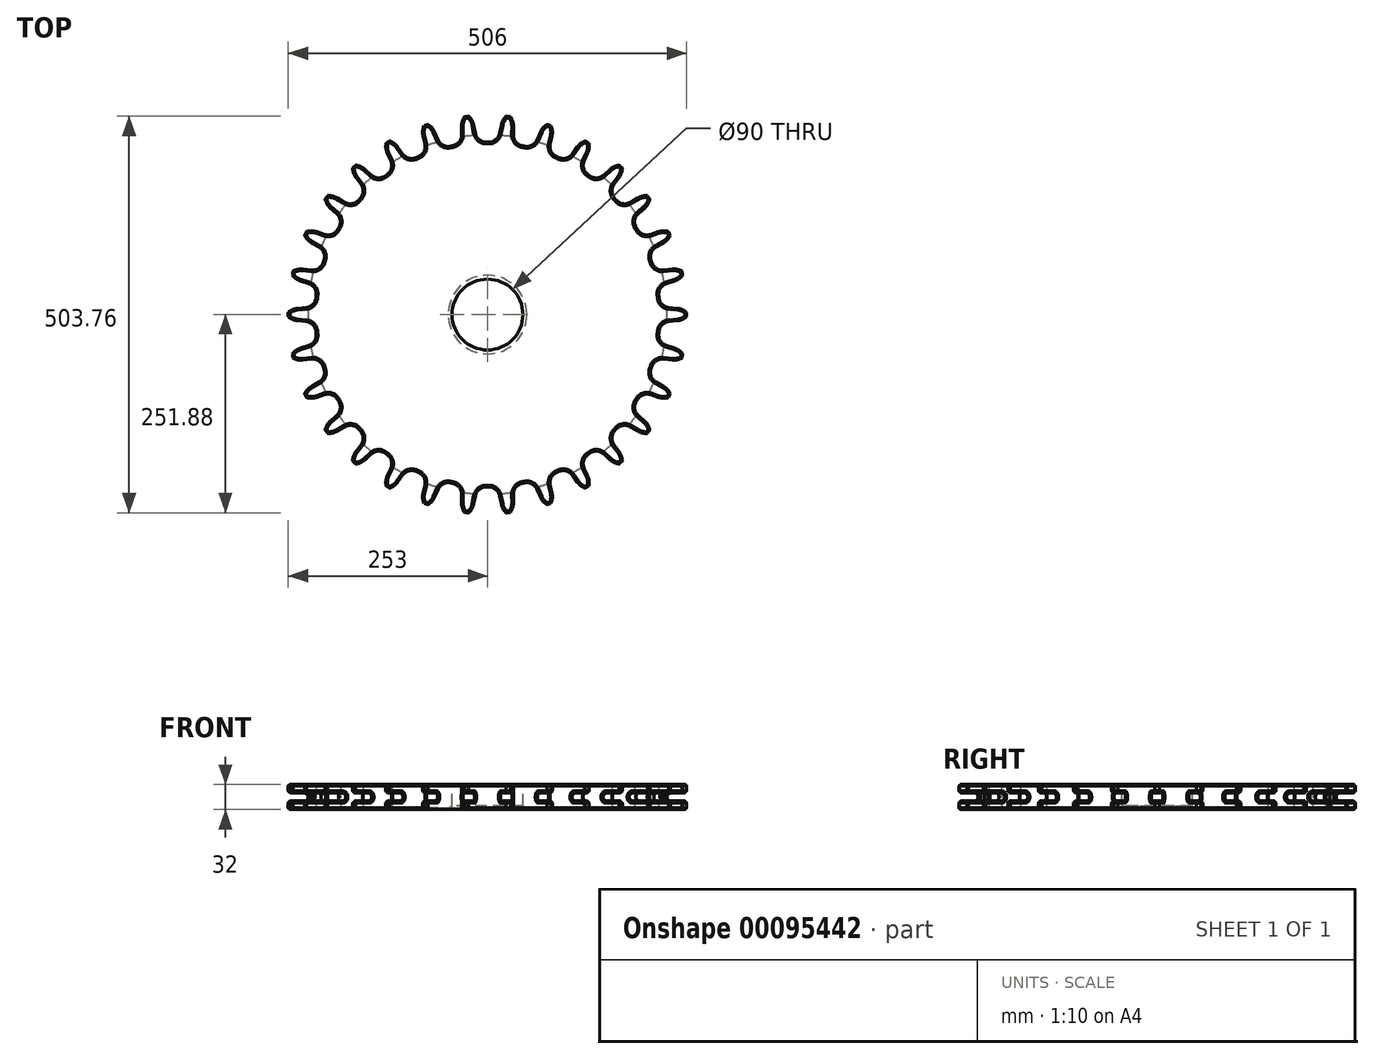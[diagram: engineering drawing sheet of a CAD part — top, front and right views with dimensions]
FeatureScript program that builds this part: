
annotation { "Feature Type Name" : "Feature", "Feature Type Description" : "" }
export const myFeature = defineFeature(function(context is Context, id is Id, definition is map)
    precondition{}
    {
        {
            var Q0;
            Q0=qCreatedBy(makeId("Top.planeOp"),FACE);
            var sketch = newSketch(context, id + "F0", { "sketchPlane" : qUnion([Q0])});
            skCircle(sketch, "E0", {"center": v(0, 0) * mm, "radius": 253 * mm});
            skCircle(sketch, "E1", {"center": v(0, 0) * mm, "radius": 216.9 * mm, "construction": true});
            skLineSegment(sketch, "E2", {"start": v(0, 0) * mm, "end": v(253, 0) * mm, "construction": true});
            skLineSegment(sketch, "E3", {"start": v(0, 0) * mm, "end": v(252.65, -13.34) * mm, "construction": true});
            skCircle(sketch, "E4", {"center": v(0, 0) * mm, "radius": 239.77 * mm, "construction": true});
            skCircle(sketch, "E5", {"center": v(239.43, -12.64) * mm, "radius": 20.44 * mm});
            skLineSegment(sketch, "E6", {"start": v(0, 0) * mm, "end": v(251.8, 24.61) * mm, "construction": true});
            skCircle(sketch, "E7", {"center": v(0, 0) * mm, "radius": 232.9 * mm, "construction": true});
            skCircle(sketch, "E8", {"center": v(231.8, 22.66) * mm, "radius": 14 * mm});
            skLineSegment(sketch, "E9", {"start": v(230.5, 8.72) * mm, "end": v(241.32, 7.72) * mm});
            skCircle(sketch, "E10", {"center": v(0, 0) * mm, "radius": 218.9 * mm});
            skSolve(sketch);
        }
        {
            var Q0;
            Q0=qCreatedBy(makeId("Top.planeOp"),FACE);
            var sketch = newSketch(context, id + "F1", { "sketchPlane" : qUnion([Q0])});
            skArc(sketch, "E11.0", {"start": v(217.86, 21.3) * mm, "mid": v(221.92, 12.73) * mm, "end": v(230.5, 8.72) * mm});
            skArc(sketch, "E12.0", {"start": v(252.99, 2.67) * mm, "mid": v(247.56, 6.12) * mm, "end": v(241.32, 7.72) * mm});
            skArc(sketch, "E13.0", {"start": v(253, 0) * mm, "mid": v(253, 1.33) * mm, "end": v(252.99, 2.67) * mm});
            skLineSegment(sketch, "E14.0", {"start": v(0, 0) * mm, "end": v(253, 0) * mm, "construction": true});
            skLineSegment(sketch, "E15.0", {"start": v(230.5, 8.72) * mm, "end": v(241.32, 7.72) * mm});
            skArc(sketch, "E16.MirrorCS", {"start": v(253, 0) * mm, "mid": v(253, -1.33) * mm, "end": v(252.99, -2.67) * mm});
            skArc(sketch, "E17.MirrorCS", {"start": v(252.99, -2.67) * mm, "mid": v(247.56, -6.12) * mm, "end": v(241.32, -7.72) * mm});
            skLineSegment(sketch, "E18.MirrorCS", {"start": v(230.5, -8.72) * mm, "end": v(241.32, -7.72) * mm});
            skArc(sketch, "E19.MirrorCS", {"start": v(217.86, -21.3) * mm, "mid": v(221.92, -12.73) * mm, "end": v(230.5, -8.72) * mm});
            skLineSegment(sketch, "E20.1.0", {"start": v(0, 0) * mm, "end": v(247.47, 52.6) * mm, "construction": true});
            skArc(sketch, "E20.1.1", {"start": v(208.68, 66.13) * mm, "mid": v(214.43, 58.6) * mm, "end": v(223.66, 56.45) * mm});
            skLineSegment(sketch, "E20.1.2", {"start": v(223.66, 56.45) * mm, "end": v(234.44, 57.72) * mm});
            skArc(sketch, "E20.1.3", {"start": v(246.9, 55.2) * mm, "mid": v(240.87, 57.46) * mm, "end": v(234.44, 57.72) * mm});
            skArc(sketch, "E20.1.4", {"start": v(247.47, 52.6) * mm, "mid": v(247.2, 53.9) * mm, "end": v(246.9, 55.2) * mm});
            skArc(sketch, "E20.1.5", {"start": v(247.47, 52.6) * mm, "mid": v(247.75, 51.3) * mm, "end": v(248.01, 50) * mm});
            skArc(sketch, "E20.1.6", {"start": v(248.01, 50) * mm, "mid": v(243.42, 45.48) * mm, "end": v(237.65, 42.63) * mm});
            skLineSegment(sketch, "E20.1.7", {"start": v(227.28, 39.4) * mm, "end": v(237.65, 42.63) * mm});
            skArc(sketch, "E20.1.8", {"start": v(217.53, 24.47) * mm, "mid": v(219.72, 33.68) * mm, "end": v(227.28, 39.4) * mm});
            skLineSegment(sketch, "E20.2.0", {"start": v(0, 0) * mm, "end": v(231.13, 102.9) * mm, "construction": true});
            skArc(sketch, "E20.2.1", {"start": v(190.37, 108.07) * mm, "mid": v(197.56, 101.9) * mm, "end": v(207.03, 101.72) * mm});
            skLineSegment(sketch, "E20.2.2", {"start": v(207.03, 101.72) * mm, "end": v(217.32, 105.2) * mm});
            skArc(sketch, "E20.2.3", {"start": v(230.03, 105.33) * mm, "mid": v(223.66, 106.28) * mm, "end": v(217.32, 105.2) * mm});
            skArc(sketch, "E20.2.4", {"start": v(231.13, 102.9) * mm, "mid": v(230.58, 104.12) * mm, "end": v(230.03, 105.33) * mm});
            skArc(sketch, "E20.2.5", {"start": v(231.13, 102.9) * mm, "mid": v(231.67, 101.69) * mm, "end": v(232.2, 100.46) * mm});
            skArc(sketch, "E20.2.6", {"start": v(232.2, 100.46) * mm, "mid": v(228.64, 95.1) * mm, "end": v(223.6, 91.1) * mm});
            skLineSegment(sketch, "E20.2.7", {"start": v(214.12, 85.8) * mm, "end": v(223.6, 91.1) * mm});
            skArc(sketch, "E20.2.8", {"start": v(207.7, 69.16) * mm, "mid": v(207.92, 78.63) * mm, "end": v(214.12, 85.8) * mm});
            skLineSegment(sketch, "E21.1.3.0", {"start": v(0, 0) * mm, "end": v(204.68, 148.7) * mm, "construction": true});
            skArc(sketch, "E21.3.3.0", {"start": v(163.74, 145.29) * mm, "mid": v(172.06, 140.75) * mm, "end": v(181.36, 142.54) * mm});
            skLineSegment(sketch, "E21.7.3.0", {"start": v(181.36, 142.54) * mm, "end": v(190.7, 148.09) * mm});
            skArc(sketch, "E21.10.3.0", {"start": v(203.1, 150.86) * mm, "mid": v(196.68, 150.46) * mm, "end": v(190.7, 148.09) * mm});
            skArc(sketch, "E21.14.3.0", {"start": v(204.68, 148.7) * mm, "mid": v(203.9, 149.79) * mm, "end": v(203.1, 150.86) * mm});
            skArc(sketch, "E21.18.3.0", {"start": v(204.68, 148.7) * mm, "mid": v(205.46, 147.63) * mm, "end": v(206.24, 146.54) * mm});
            skArc(sketch, "E21.22.3.0", {"start": v(206.24, 146.54) * mm, "mid": v(203.87, 140.56) * mm, "end": v(199.77, 135.6) * mm});
            skLineSegment(sketch, "E21.26.3.0", {"start": v(191.6, 128.44) * mm, "end": v(199.77, 135.6) * mm});
            skArc(sketch, "E21.29.3.0", {"start": v(188.77, 110.83) * mm, "mid": v(187.02, 120.14) * mm, "end": v(191.6, 128.44) * mm});
            skLineSegment(sketch, "E21.1.4.0", {"start": v(0, 0) * mm, "end": v(169.3, 188.02) * mm, "construction": true});
            skArc(sketch, "E21.3.4.0", {"start": v(129.95, 176.16) * mm, "mid": v(139.03, 173.44) * mm, "end": v(147.76, 177.13) * mm});
            skLineSegment(sketch, "E21.7.4.0", {"start": v(147.76, 177.13) * mm, "end": v(155.74, 184.5) * mm});
            skArc(sketch, "E21.10.4.0", {"start": v(167.3, 189.79) * mm, "mid": v(161.1, 188.07) * mm, "end": v(155.74, 184.5) * mm});
            skArc(sketch, "E21.14.4.0", {"start": v(169.3, 188.02) * mm, "mid": v(168.3, 188.9) * mm, "end": v(167.3, 189.79) * mm});
            skArc(sketch, "E21.18.4.0", {"start": v(169.3, 188.02) * mm, "mid": v(170.28, 187.12) * mm, "end": v(171.26, 186.22) * mm});
            skArc(sketch, "E21.22.4.0", {"start": v(171.26, 186.22) * mm, "mid": v(170.2, 179.87) * mm, "end": v(167.2, 174.17) * mm});
            skLineSegment(sketch, "E21.26.4.0", {"start": v(160.72, 165.47) * mm, "end": v(167.2, 174.17) * mm});
            skArc(sketch, "E21.29.4.0", {"start": v(161.6, 147.65) * mm, "mid": v(157.96, 156.4) * mm, "end": v(160.72, 165.47) * mm});
            skLineSegment(sketch, "E21.1.5.0", {"start": v(0, 0) * mm, "end": v(126.5, 219.1) * mm, "construction": true});
            skArc(sketch, "E21.3.5.0", {"start": v(90.49, 199.32) * mm, "mid": v(99.93, 198.56) * mm, "end": v(107.7, 203.98) * mm});
            skLineSegment(sketch, "E21.7.5.0", {"start": v(107.7, 203.98) * mm, "end": v(113.98, 212.85) * mm});
            skArc(sketch, "E21.10.5.0", {"start": v(124.18, 220.43) * mm, "mid": v(118.48, 217.45) * mm, "end": v(113.98, 212.85) * mm});
            skArc(sketch, "E21.14.5.0", {"start": v(126.5, 219.1) * mm, "mid": v(125.34, 219.77) * mm, "end": v(124.18, 220.43) * mm});
            skArc(sketch, "E21.18.5.0", {"start": v(126.5, 219.1) * mm, "mid": v(127.65, 218.43) * mm, "end": v(128.8, 217.76) * mm});
            skArc(sketch, "E21.22.5.0", {"start": v(128.8, 217.76) * mm, "mid": v(129.08, 211.33) * mm, "end": v(127.34, 205.13) * mm});
            skLineSegment(sketch, "E21.26.5.0", {"start": v(122.8, 195.27) * mm, "end": v(127.34, 205.13) * mm});
            skArc(sketch, "E21.29.5.0", {"start": v(127.38, 178.03) * mm, "mid": v(121.99, 185.82) * mm, "end": v(122.8, 195.27) * mm});
            skLineSegment(sketch, "E22.1.6.0", {"start": v(0, 0) * mm, "end": v(78.18, 240.62) * mm, "construction": true});
            skArc(sketch, "E22.3.6.0", {"start": v(47.07, 213.78) * mm, "mid": v(56.47, 215) * mm, "end": v(62.94, 221.92) * mm});
            skLineSegment(sketch, "E22.7.6.0", {"start": v(62.94, 221.92) * mm, "end": v(67.23, 231.9) * mm});
            skArc(sketch, "E22.10.6.0", {"start": v(75.64, 241.43) * mm, "mid": v(70.68, 237.33) * mm, "end": v(67.23, 231.9) * mm});
            skArc(sketch, "E22.14.6.0", {"start": v(78.18, 240.62) * mm, "mid": v(76.91, 241.03) * mm, "end": v(75.64, 241.43) * mm});
            skArc(sketch, "E22.18.6.0", {"start": v(78.18, 240.62) * mm, "mid": v(79.45, 240.2) * mm, "end": v(80.71, 239.78) * mm});
            skArc(sketch, "E22.22.6.0", {"start": v(80.71, 239.78) * mm, "mid": v(82.32, 233.55) * mm, "end": v(81.91, 227.12) * mm});
            skLineSegment(sketch, "E22.26.6.0", {"start": v(79.52, 216.53) * mm, "end": v(81.91, 227.12) * mm});
            skArc(sketch, "E22.29.6.0", {"start": v(87.58, 200.62) * mm, "mid": v(80.69, 207.13) * mm, "end": v(79.52, 216.53) * mm});
            skLineSegment(sketch, "E22.1.7.0", {"start": v(0, 0) * mm, "end": v(26.45, 251.61) * mm, "construction": true});
            skArc(sketch, "E22.3.7.0", {"start": v(1.6, 218.9) * mm, "mid": v(10.53, 222.04) * mm, "end": v(15.42, 230.16) * mm});
            skLineSegment(sketch, "E22.7.7.0", {"start": v(15.42, 230.16) * mm, "end": v(17.55, 240.8) * mm});
            skArc(sketch, "E22.10.7.0", {"start": v(23.8, 251.88) * mm, "mid": v(19.79, 246.84) * mm, "end": v(17.55, 240.8) * mm});
            skArc(sketch, "E22.14.7.0", {"start": v(26.45, 251.61) * mm, "mid": v(25.12, 251.75) * mm, "end": v(23.8, 251.88) * mm});
            skArc(sketch, "E22.18.7.0", {"start": v(26.45, 251.61) * mm, "mid": v(27.77, 251.47) * mm, "end": v(29.1, 251.32) * mm});
            skArc(sketch, "E22.22.7.0", {"start": v(29.1, 251.32) * mm, "mid": v(31.96, 245.56) * mm, "end": v(32.9, 239.2) * mm});
            skLineSegment(sketch, "E22.26.7.0", {"start": v(32.77, 228.33) * mm, "end": v(32.9, 239.2) * mm});
            skArc(sketch, "E22.29.7.0", {"start": v(43.95, 214.45) * mm, "mid": v(35.86, 219.38) * mm, "end": v(32.77, 228.33) * mm});
            skLineSegment(sketch, "E22.1.8.0", {"start": v(0, 0) * mm, "end": v(-26.45, 251.61) * mm, "construction": true});
            skArc(sketch, "E22.3.8.0", {"start": v(-43.95, 214.45) * mm, "mid": v(-35.86, 219.38) * mm, "end": v(-32.77, 228.33) * mm});
            skLineSegment(sketch, "E22.7.8.0", {"start": v(-32.77, 228.33) * mm, "end": v(-32.9, 239.2) * mm});
            skArc(sketch, "E22.10.8.0", {"start": v(-29.1, 251.32) * mm, "mid": v(-31.96, 245.56) * mm, "end": v(-32.9, 239.2) * mm});
            skArc(sketch, "E22.14.8.0", {"start": v(-26.45, 251.61) * mm, "mid": v(-27.77, 251.47) * mm, "end": v(-29.1, 251.32) * mm});
            skArc(sketch, "E22.18.8.0", {"start": v(-26.45, 251.61) * mm, "mid": v(-25.12, 251.75) * mm, "end": v(-23.8, 251.88) * mm});
            skArc(sketch, "E22.22.8.0", {"start": v(-23.8, 251.88) * mm, "mid": v(-19.79, 246.84) * mm, "end": v(-17.55, 240.8) * mm});
            skLineSegment(sketch, "E22.26.8.0", {"start": v(-15.42, 230.16) * mm, "end": v(-17.55, 240.8) * mm});
            skArc(sketch, "E22.29.8.0", {"start": v(-1.6, 218.9) * mm, "mid": v(-10.53, 222.04) * mm, "end": v(-15.42, 230.16) * mm});
            skLineSegment(sketch, "E22.1.9.0", {"start": v(0, 0) * mm, "end": v(-78.18, 240.62) * mm, "construction": true});
            skArc(sketch, "E22.3.9.0", {"start": v(-87.58, 200.62) * mm, "mid": v(-80.69, 207.13) * mm, "end": v(-79.52, 216.53) * mm});
            skLineSegment(sketch, "E22.7.9.0", {"start": v(-79.52, 216.53) * mm, "end": v(-81.91, 227.12) * mm});
            skArc(sketch, "E22.10.9.0", {"start": v(-80.71, 239.78) * mm, "mid": v(-82.32, 233.55) * mm, "end": v(-81.91, 227.12) * mm});
            skArc(sketch, "E22.14.9.0", {"start": v(-78.18, 240.62) * mm, "mid": v(-79.45, 240.2) * mm, "end": v(-80.71, 239.78) * mm});
            skArc(sketch, "E22.18.9.0", {"start": v(-78.18, 240.62) * mm, "mid": v(-76.91, 241.03) * mm, "end": v(-75.64, 241.43) * mm});
            skArc(sketch, "E22.22.9.0", {"start": v(-75.64, 241.43) * mm, "mid": v(-70.68, 237.33) * mm, "end": v(-67.23, 231.9) * mm});
            skLineSegment(sketch, "E22.26.9.0", {"start": v(-62.94, 221.92) * mm, "end": v(-67.23, 231.9) * mm});
            skArc(sketch, "E22.29.9.0", {"start": v(-47.07, 213.78) * mm, "mid": v(-56.47, 215) * mm, "end": v(-62.94, 221.92) * mm});
            skLineSegment(sketch, "E22.1.10.0", {"start": v(0, 0) * mm, "end": v(-126.5, 219.1) * mm, "construction": true});
            skArc(sketch, "E22.3.10.0", {"start": v(-127.38, 178.03) * mm, "mid": v(-121.99, 185.82) * mm, "end": v(-122.8, 195.27) * mm});
            skLineSegment(sketch, "E22.7.10.0", {"start": v(-122.8, 195.27) * mm, "end": v(-127.34, 205.13) * mm});
            skArc(sketch, "E22.10.10.0", {"start": v(-128.8, 217.76) * mm, "mid": v(-129.08, 211.33) * mm, "end": v(-127.34, 205.13) * mm});
            skArc(sketch, "E22.14.10.0", {"start": v(-126.5, 219.1) * mm, "mid": v(-127.65, 218.43) * mm, "end": v(-128.8, 217.76) * mm});
            skArc(sketch, "E22.18.10.0", {"start": v(-126.5, 219.1) * mm, "mid": v(-125.34, 219.77) * mm, "end": v(-124.18, 220.43) * mm});
            skArc(sketch, "E22.22.10.0", {"start": v(-124.18, 220.43) * mm, "mid": v(-118.48, 217.45) * mm, "end": v(-113.98, 212.85) * mm});
            skLineSegment(sketch, "E22.26.10.0", {"start": v(-107.7, 203.98) * mm, "end": v(-113.98, 212.85) * mm});
            skArc(sketch, "E22.29.10.0", {"start": v(-90.49, 199.32) * mm, "mid": v(-99.93, 198.56) * mm, "end": v(-107.7, 203.98) * mm});
            skLineSegment(sketch, "E22.1.11.0", {"start": v(0, 0) * mm, "end": v(-169.3, 188.02) * mm, "construction": true});
            skArc(sketch, "E22.3.11.0", {"start": v(-161.6, 147.65) * mm, "mid": v(-157.96, 156.4) * mm, "end": v(-160.72, 165.47) * mm});
            skLineSegment(sketch, "E22.7.11.0", {"start": v(-160.72, 165.47) * mm, "end": v(-167.2, 174.17) * mm});
            skArc(sketch, "E22.10.11.0", {"start": v(-171.26, 186.22) * mm, "mid": v(-170.2, 179.87) * mm, "end": v(-167.2, 174.17) * mm});
            skArc(sketch, "E22.14.11.0", {"start": v(-169.3, 188.02) * mm, "mid": v(-170.28, 187.12) * mm, "end": v(-171.26, 186.22) * mm});
            skArc(sketch, "E22.18.11.0", {"start": v(-169.3, 188.02) * mm, "mid": v(-168.3, 188.9) * mm, "end": v(-167.3, 189.79) * mm});
            skArc(sketch, "E22.22.11.0", {"start": v(-167.3, 189.79) * mm, "mid": v(-161.1, 188.07) * mm, "end": v(-155.74, 184.5) * mm});
            skLineSegment(sketch, "E22.26.11.0", {"start": v(-147.76, 177.13) * mm, "end": v(-155.74, 184.5) * mm});
            skArc(sketch, "E22.29.11.0", {"start": v(-129.95, 176.16) * mm, "mid": v(-139.03, 173.44) * mm, "end": v(-147.76, 177.13) * mm});
            skLineSegment(sketch, "E22.1.12.0", {"start": v(0, 0) * mm, "end": v(-204.68, 148.7) * mm, "construction": true});
            skArc(sketch, "E22.3.12.0", {"start": v(-188.77, 110.83) * mm, "mid": v(-187.02, 120.14) * mm, "end": v(-191.6, 128.44) * mm});
            skLineSegment(sketch, "E22.7.12.0", {"start": v(-191.6, 128.44) * mm, "end": v(-199.77, 135.6) * mm});
            skArc(sketch, "E22.10.12.0", {"start": v(-206.24, 146.54) * mm, "mid": v(-203.87, 140.56) * mm, "end": v(-199.77, 135.6) * mm});
            skArc(sketch, "E22.14.12.0", {"start": v(-204.68, 148.7) * mm, "mid": v(-205.46, 147.63) * mm, "end": v(-206.24, 146.54) * mm});
            skArc(sketch, "E22.18.12.0", {"start": v(-204.68, 148.7) * mm, "mid": v(-203.9, 149.79) * mm, "end": v(-203.1, 150.86) * mm});
            skArc(sketch, "E22.22.12.0", {"start": v(-203.1, 150.86) * mm, "mid": v(-196.68, 150.46) * mm, "end": v(-190.7, 148.09) * mm});
            skLineSegment(sketch, "E22.26.12.0", {"start": v(-181.36, 142.54) * mm, "end": v(-190.7, 148.09) * mm});
            skArc(sketch, "E22.29.12.0", {"start": v(-163.74, 145.29) * mm, "mid": v(-172.06, 140.75) * mm, "end": v(-181.36, 142.54) * mm});
            skLineSegment(sketch, "E22.1.13.0", {"start": v(0, 0) * mm, "end": v(-231.13, 102.9) * mm, "construction": true});
            skArc(sketch, "E22.3.13.0", {"start": v(-207.7, 69.16) * mm, "mid": v(-207.92, 78.63) * mm, "end": v(-214.12, 85.8) * mm});
            skLineSegment(sketch, "E22.7.13.0", {"start": v(-214.12, 85.8) * mm, "end": v(-223.6, 91.1) * mm});
            skArc(sketch, "E22.10.13.0", {"start": v(-232.2, 100.46) * mm, "mid": v(-228.64, 95.1) * mm, "end": v(-223.6, 91.1) * mm});
            skArc(sketch, "E22.14.13.0", {"start": v(-231.13, 102.9) * mm, "mid": v(-231.67, 101.69) * mm, "end": v(-232.2, 100.46) * mm});
            skArc(sketch, "E22.18.13.0", {"start": v(-231.13, 102.9) * mm, "mid": v(-230.58, 104.12) * mm, "end": v(-230.03, 105.33) * mm});
            skArc(sketch, "E22.22.13.0", {"start": v(-230.03, 105.33) * mm, "mid": v(-223.66, 106.28) * mm, "end": v(-217.32, 105.2) * mm});
            skLineSegment(sketch, "E22.26.13.0", {"start": v(-207.03, 101.72) * mm, "end": v(-217.32, 105.2) * mm});
            skArc(sketch, "E22.29.13.0", {"start": v(-190.37, 108.07) * mm, "mid": v(-197.56, 101.9) * mm, "end": v(-207.03, 101.72) * mm});
            skLineSegment(sketch, "E22.1.14.0", {"start": v(0, 0) * mm, "end": v(-247.47, 52.6) * mm, "construction": true});
            skArc(sketch, "E22.3.14.0", {"start": v(-217.53, 24.47) * mm, "mid": v(-219.72, 33.68) * mm, "end": v(-227.28, 39.4) * mm});
            skLineSegment(sketch, "E22.7.14.0", {"start": v(-227.28, 39.4) * mm, "end": v(-237.65, 42.63) * mm});
            skArc(sketch, "E22.10.14.0", {"start": v(-248.01, 50) * mm, "mid": v(-243.42, 45.48) * mm, "end": v(-237.65, 42.63) * mm});
            skArc(sketch, "E22.14.14.0", {"start": v(-247.47, 52.6) * mm, "mid": v(-247.75, 51.3) * mm, "end": v(-248.01, 50) * mm});
            skArc(sketch, "E22.18.14.0", {"start": v(-247.47, 52.6) * mm, "mid": v(-247.2, 53.9) * mm, "end": v(-246.9, 55.2) * mm});
            skArc(sketch, "E22.22.14.0", {"start": v(-246.9, 55.2) * mm, "mid": v(-240.87, 57.46) * mm, "end": v(-234.44, 57.72) * mm});
            skLineSegment(sketch, "E22.26.14.0", {"start": v(-223.66, 56.45) * mm, "end": v(-234.44, 57.72) * mm});
            skArc(sketch, "E22.29.14.0", {"start": v(-208.68, 66.13) * mm, "mid": v(-214.43, 58.6) * mm, "end": v(-223.66, 56.45) * mm});
            skLineSegment(sketch, "E22.1.15.0", {"start": v(0, 0) * mm, "end": v(-253, 0) * mm, "construction": true});
            skArc(sketch, "E22.3.15.0", {"start": v(-217.86, -21.3) * mm, "mid": v(-221.92, -12.73) * mm, "end": v(-230.5, -8.72) * mm});
            skLineSegment(sketch, "E22.7.15.0", {"start": v(-230.5, -8.72) * mm, "end": v(-241.32, -7.72) * mm});
            skArc(sketch, "E22.10.15.0", {"start": v(-252.99, -2.67) * mm, "mid": v(-247.56, -6.12) * mm, "end": v(-241.32, -7.72) * mm});
            skArc(sketch, "E22.14.15.0", {"start": v(-253, 0) * mm, "mid": v(-253, -1.33) * mm, "end": v(-252.99, -2.67) * mm});
            skArc(sketch, "E22.18.15.0", {"start": v(-253, 0) * mm, "mid": v(-253, 1.33) * mm, "end": v(-252.99, 2.67) * mm});
            skArc(sketch, "E22.22.15.0", {"start": v(-252.99, 2.67) * mm, "mid": v(-247.56, 6.12) * mm, "end": v(-241.32, 7.72) * mm});
            skLineSegment(sketch, "E22.26.15.0", {"start": v(-230.5, 8.72) * mm, "end": v(-241.32, 7.72) * mm});
            skArc(sketch, "E22.29.15.0", {"start": v(-217.86, 21.3) * mm, "mid": v(-221.92, 12.73) * mm, "end": v(-230.5, 8.72) * mm});
            skLineSegment(sketch, "E22.1.16.0", {"start": v(0, 0) * mm, "end": v(-247.47, -52.6) * mm, "construction": true});
            skArc(sketch, "E22.3.16.0", {"start": v(-208.68, -66.13) * mm, "mid": v(-214.43, -58.6) * mm, "end": v(-223.66, -56.45) * mm});
            skLineSegment(sketch, "E22.7.16.0", {"start": v(-223.66, -56.45) * mm, "end": v(-234.44, -57.72) * mm});
            skArc(sketch, "E22.10.16.0", {"start": v(-246.9, -55.2) * mm, "mid": v(-240.87, -57.46) * mm, "end": v(-234.44, -57.72) * mm});
            skArc(sketch, "E22.14.16.0", {"start": v(-247.47, -52.6) * mm, "mid": v(-247.2, -53.9) * mm, "end": v(-246.9, -55.2) * mm});
            skArc(sketch, "E22.18.16.0", {"start": v(-247.47, -52.6) * mm, "mid": v(-247.75, -51.3) * mm, "end": v(-248.01, -50) * mm});
            skArc(sketch, "E22.22.16.0", {"start": v(-248.01, -50) * mm, "mid": v(-243.42, -45.48) * mm, "end": v(-237.65, -42.63) * mm});
            skLineSegment(sketch, "E22.26.16.0", {"start": v(-227.28, -39.4) * mm, "end": v(-237.65, -42.63) * mm});
            skArc(sketch, "E22.29.16.0", {"start": v(-217.53, -24.47) * mm, "mid": v(-219.72, -33.68) * mm, "end": v(-227.28, -39.4) * mm});
            skLineSegment(sketch, "E22.1.17.0", {"start": v(0, 0) * mm, "end": v(-231.13, -102.9) * mm, "construction": true});
            skArc(sketch, "E22.3.17.0", {"start": v(-190.37, -108.07) * mm, "mid": v(-197.56, -101.9) * mm, "end": v(-207.03, -101.72) * mm});
            skLineSegment(sketch, "E22.7.17.0", {"start": v(-207.03, -101.72) * mm, "end": v(-217.32, -105.2) * mm});
            skArc(sketch, "E22.10.17.0", {"start": v(-230.03, -105.33) * mm, "mid": v(-223.66, -106.28) * mm, "end": v(-217.32, -105.2) * mm});
            skArc(sketch, "E22.14.17.0", {"start": v(-231.13, -102.9) * mm, "mid": v(-230.58, -104.12) * mm, "end": v(-230.03, -105.33) * mm});
            skArc(sketch, "E22.18.17.0", {"start": v(-231.13, -102.9) * mm, "mid": v(-231.67, -101.69) * mm, "end": v(-232.2, -100.46) * mm});
            skArc(sketch, "E22.22.17.0", {"start": v(-232.2, -100.46) * mm, "mid": v(-228.64, -95.1) * mm, "end": v(-223.6, -91.1) * mm});
            skLineSegment(sketch, "E22.26.17.0", {"start": v(-214.12, -85.8) * mm, "end": v(-223.6, -91.1) * mm});
            skArc(sketch, "E22.29.17.0", {"start": v(-207.7, -69.16) * mm, "mid": v(-207.92, -78.63) * mm, "end": v(-214.12, -85.8) * mm});
            skLineSegment(sketch, "E22.1.18.0", {"start": v(0, 0) * mm, "end": v(-204.68, -148.7) * mm, "construction": true});
            skArc(sketch, "E22.3.18.0", {"start": v(-163.74, -145.29) * mm, "mid": v(-172.06, -140.75) * mm, "end": v(-181.36, -142.54) * mm});
            skLineSegment(sketch, "E22.7.18.0", {"start": v(-181.36, -142.54) * mm, "end": v(-190.7, -148.09) * mm});
            skArc(sketch, "E22.10.18.0", {"start": v(-203.1, -150.86) * mm, "mid": v(-196.68, -150.46) * mm, "end": v(-190.7, -148.09) * mm});
            skArc(sketch, "E22.14.18.0", {"start": v(-204.68, -148.7) * mm, "mid": v(-203.9, -149.79) * mm, "end": v(-203.1, -150.86) * mm});
            skArc(sketch, "E22.18.18.0", {"start": v(-204.68, -148.7) * mm, "mid": v(-205.46, -147.63) * mm, "end": v(-206.24, -146.54) * mm});
            skArc(sketch, "E22.22.18.0", {"start": v(-206.24, -146.54) * mm, "mid": v(-203.87, -140.56) * mm, "end": v(-199.77, -135.6) * mm});
            skLineSegment(sketch, "E22.26.18.0", {"start": v(-191.6, -128.44) * mm, "end": v(-199.77, -135.6) * mm});
            skArc(sketch, "E22.29.18.0", {"start": v(-188.77, -110.83) * mm, "mid": v(-187.02, -120.14) * mm, "end": v(-191.6, -128.44) * mm});
            skLineSegment(sketch, "E22.1.19.0", {"start": v(0, 0) * mm, "end": v(-169.3, -188.02) * mm, "construction": true});
            skArc(sketch, "E22.3.19.0", {"start": v(-129.95, -176.16) * mm, "mid": v(-139.03, -173.44) * mm, "end": v(-147.76, -177.13) * mm});
            skLineSegment(sketch, "E22.7.19.0", {"start": v(-147.76, -177.13) * mm, "end": v(-155.74, -184.5) * mm});
            skArc(sketch, "E22.10.19.0", {"start": v(-167.3, -189.79) * mm, "mid": v(-161.1, -188.07) * mm, "end": v(-155.74, -184.5) * mm});
            skArc(sketch, "E22.14.19.0", {"start": v(-169.3, -188.02) * mm, "mid": v(-168.3, -188.9) * mm, "end": v(-167.3, -189.79) * mm});
            skArc(sketch, "E22.18.19.0", {"start": v(-169.3, -188.02) * mm, "mid": v(-170.28, -187.12) * mm, "end": v(-171.26, -186.22) * mm});
            skArc(sketch, "E22.22.19.0", {"start": v(-171.26, -186.22) * mm, "mid": v(-170.2, -179.87) * mm, "end": v(-167.2, -174.17) * mm});
            skLineSegment(sketch, "E22.26.19.0", {"start": v(-160.72, -165.47) * mm, "end": v(-167.2, -174.17) * mm});
            skArc(sketch, "E22.29.19.0", {"start": v(-161.6, -147.65) * mm, "mid": v(-157.96, -156.4) * mm, "end": v(-160.72, -165.47) * mm});
            skLineSegment(sketch, "E22.1.20.0", {"start": v(0, 0) * mm, "end": v(-126.5, -219.1) * mm, "construction": true});
            skArc(sketch, "E22.3.20.0", {"start": v(-90.49, -199.32) * mm, "mid": v(-99.93, -198.56) * mm, "end": v(-107.7, -203.98) * mm});
            skLineSegment(sketch, "E22.7.20.0", {"start": v(-107.7, -203.98) * mm, "end": v(-113.98, -212.85) * mm});
            skArc(sketch, "E22.10.20.0", {"start": v(-124.18, -220.43) * mm, "mid": v(-118.48, -217.45) * mm, "end": v(-113.98, -212.85) * mm});
            skArc(sketch, "E22.14.20.0", {"start": v(-126.5, -219.1) * mm, "mid": v(-125.34, -219.77) * mm, "end": v(-124.18, -220.43) * mm});
            skArc(sketch, "E22.18.20.0", {"start": v(-126.5, -219.1) * mm, "mid": v(-127.65, -218.43) * mm, "end": v(-128.8, -217.76) * mm});
            skArc(sketch, "E22.22.20.0", {"start": v(-128.8, -217.76) * mm, "mid": v(-129.08, -211.33) * mm, "end": v(-127.34, -205.13) * mm});
            skLineSegment(sketch, "E22.26.20.0", {"start": v(-122.8, -195.27) * mm, "end": v(-127.34, -205.13) * mm});
            skArc(sketch, "E22.29.20.0", {"start": v(-127.38, -178.03) * mm, "mid": v(-121.99, -185.82) * mm, "end": v(-122.8, -195.27) * mm});
            skLineSegment(sketch, "E22.1.21.0", {"start": v(0, 0) * mm, "end": v(-78.18, -240.62) * mm, "construction": true});
            skArc(sketch, "E22.3.21.0", {"start": v(-47.07, -213.78) * mm, "mid": v(-56.47, -215) * mm, "end": v(-62.94, -221.92) * mm});
            skLineSegment(sketch, "E22.7.21.0", {"start": v(-62.94, -221.92) * mm, "end": v(-67.23, -231.9) * mm});
            skArc(sketch, "E22.10.21.0", {"start": v(-75.64, -241.43) * mm, "mid": v(-70.68, -237.33) * mm, "end": v(-67.23, -231.9) * mm});
            skArc(sketch, "E22.14.21.0", {"start": v(-78.18, -240.62) * mm, "mid": v(-76.91, -241.03) * mm, "end": v(-75.64, -241.43) * mm});
            skArc(sketch, "E22.18.21.0", {"start": v(-78.18, -240.62) * mm, "mid": v(-79.45, -240.2) * mm, "end": v(-80.71, -239.78) * mm});
            skArc(sketch, "E22.22.21.0", {"start": v(-80.71, -239.78) * mm, "mid": v(-82.32, -233.55) * mm, "end": v(-81.91, -227.12) * mm});
            skLineSegment(sketch, "E22.26.21.0", {"start": v(-79.52, -216.53) * mm, "end": v(-81.91, -227.12) * mm});
            skArc(sketch, "E22.29.21.0", {"start": v(-87.58, -200.62) * mm, "mid": v(-80.69, -207.13) * mm, "end": v(-79.52, -216.53) * mm});
            skLineSegment(sketch, "E22.1.22.0", {"start": v(0, 0) * mm, "end": v(-26.45, -251.61) * mm, "construction": true});
            skArc(sketch, "E22.3.22.0", {"start": v(-1.6, -218.9) * mm, "mid": v(-10.53, -222.04) * mm, "end": v(-15.42, -230.16) * mm});
            skLineSegment(sketch, "E22.7.22.0", {"start": v(-15.42, -230.16) * mm, "end": v(-17.55, -240.8) * mm});
            skArc(sketch, "E22.10.22.0", {"start": v(-23.8, -251.88) * mm, "mid": v(-19.79, -246.84) * mm, "end": v(-17.55, -240.8) * mm});
            skArc(sketch, "E22.14.22.0", {"start": v(-26.45, -251.61) * mm, "mid": v(-25.12, -251.75) * mm, "end": v(-23.8, -251.88) * mm});
            skArc(sketch, "E22.18.22.0", {"start": v(-26.45, -251.61) * mm, "mid": v(-27.77, -251.47) * mm, "end": v(-29.1, -251.32) * mm});
            skArc(sketch, "E22.22.22.0", {"start": v(-29.1, -251.32) * mm, "mid": v(-31.96, -245.56) * mm, "end": v(-32.9, -239.2) * mm});
            skLineSegment(sketch, "E22.26.22.0", {"start": v(-32.77, -228.33) * mm, "end": v(-32.9, -239.2) * mm});
            skArc(sketch, "E22.29.22.0", {"start": v(-43.95, -214.45) * mm, "mid": v(-35.86, -219.38) * mm, "end": v(-32.77, -228.33) * mm});
            skLineSegment(sketch, "E22.1.23.0", {"start": v(0, 0) * mm, "end": v(26.45, -251.61) * mm, "construction": true});
            skArc(sketch, "E22.3.23.0", {"start": v(43.95, -214.45) * mm, "mid": v(35.86, -219.38) * mm, "end": v(32.77, -228.33) * mm});
            skLineSegment(sketch, "E22.7.23.0", {"start": v(32.77, -228.33) * mm, "end": v(32.9, -239.2) * mm});
            skArc(sketch, "E22.10.23.0", {"start": v(29.1, -251.32) * mm, "mid": v(31.96, -245.56) * mm, "end": v(32.9, -239.2) * mm});
            skArc(sketch, "E22.14.23.0", {"start": v(26.45, -251.61) * mm, "mid": v(27.77, -251.47) * mm, "end": v(29.1, -251.32) * mm});
            skArc(sketch, "E22.18.23.0", {"start": v(26.45, -251.61) * mm, "mid": v(25.12, -251.75) * mm, "end": v(23.8, -251.88) * mm});
            skArc(sketch, "E22.22.23.0", {"start": v(23.8, -251.88) * mm, "mid": v(19.79, -246.84) * mm, "end": v(17.55, -240.8) * mm});
            skLineSegment(sketch, "E22.26.23.0", {"start": v(15.42, -230.16) * mm, "end": v(17.55, -240.8) * mm});
            skArc(sketch, "E22.29.23.0", {"start": v(1.6, -218.9) * mm, "mid": v(10.53, -222.04) * mm, "end": v(15.42, -230.16) * mm});
            skLineSegment(sketch, "E22.1.24.0", {"start": v(0, 0) * mm, "end": v(78.18, -240.62) * mm, "construction": true});
            skArc(sketch, "E22.3.24.0", {"start": v(87.58, -200.62) * mm, "mid": v(80.69, -207.13) * mm, "end": v(79.52, -216.53) * mm});
            skLineSegment(sketch, "E22.7.24.0", {"start": v(79.52, -216.53) * mm, "end": v(81.91, -227.12) * mm});
            skArc(sketch, "E22.10.24.0", {"start": v(80.71, -239.78) * mm, "mid": v(82.32, -233.55) * mm, "end": v(81.91, -227.12) * mm});
            skArc(sketch, "E22.14.24.0", {"start": v(78.18, -240.62) * mm, "mid": v(79.45, -240.2) * mm, "end": v(80.71, -239.78) * mm});
            skArc(sketch, "E22.18.24.0", {"start": v(78.18, -240.62) * mm, "mid": v(76.91, -241.03) * mm, "end": v(75.64, -241.43) * mm});
            skArc(sketch, "E22.22.24.0", {"start": v(75.64, -241.43) * mm, "mid": v(70.68, -237.33) * mm, "end": v(67.23, -231.9) * mm});
            skLineSegment(sketch, "E22.26.24.0", {"start": v(62.94, -221.92) * mm, "end": v(67.23, -231.9) * mm});
            skArc(sketch, "E22.29.24.0", {"start": v(47.07, -213.78) * mm, "mid": v(56.47, -215) * mm, "end": v(62.94, -221.92) * mm});
            skLineSegment(sketch, "E22.1.25.0", {"start": v(0, 0) * mm, "end": v(126.5, -219.1) * mm, "construction": true});
            skArc(sketch, "E22.3.25.0", {"start": v(127.38, -178.03) * mm, "mid": v(121.99, -185.82) * mm, "end": v(122.8, -195.27) * mm});
            skLineSegment(sketch, "E22.7.25.0", {"start": v(122.8, -195.27) * mm, "end": v(127.34, -205.13) * mm});
            skArc(sketch, "E22.10.25.0", {"start": v(128.8, -217.76) * mm, "mid": v(129.08, -211.33) * mm, "end": v(127.34, -205.13) * mm});
            skArc(sketch, "E22.14.25.0", {"start": v(126.5, -219.1) * mm, "mid": v(127.65, -218.43) * mm, "end": v(128.8, -217.76) * mm});
            skArc(sketch, "E22.18.25.0", {"start": v(126.5, -219.1) * mm, "mid": v(125.34, -219.77) * mm, "end": v(124.18, -220.43) * mm});
            skArc(sketch, "E22.22.25.0", {"start": v(124.18, -220.43) * mm, "mid": v(118.48, -217.45) * mm, "end": v(113.98, -212.85) * mm});
            skLineSegment(sketch, "E22.26.25.0", {"start": v(107.7, -203.98) * mm, "end": v(113.98, -212.85) * mm});
            skArc(sketch, "E22.29.25.0", {"start": v(90.49, -199.32) * mm, "mid": v(99.93, -198.56) * mm, "end": v(107.7, -203.98) * mm});
            skLineSegment(sketch, "E22.1.26.0", {"start": v(0, 0) * mm, "end": v(169.3, -188.02) * mm, "construction": true});
            skArc(sketch, "E22.3.26.0", {"start": v(161.6, -147.65) * mm, "mid": v(157.96, -156.4) * mm, "end": v(160.72, -165.47) * mm});
            skLineSegment(sketch, "E22.7.26.0", {"start": v(160.72, -165.47) * mm, "end": v(167.2, -174.17) * mm});
            skArc(sketch, "E22.10.26.0", {"start": v(171.26, -186.22) * mm, "mid": v(170.2, -179.87) * mm, "end": v(167.2, -174.17) * mm});
            skArc(sketch, "E22.14.26.0", {"start": v(169.3, -188.02) * mm, "mid": v(170.28, -187.12) * mm, "end": v(171.26, -186.22) * mm});
            skArc(sketch, "E22.18.26.0", {"start": v(169.3, -188.02) * mm, "mid": v(168.3, -188.9) * mm, "end": v(167.3, -189.79) * mm});
            skArc(sketch, "E22.22.26.0", {"start": v(167.3, -189.79) * mm, "mid": v(161.1, -188.07) * mm, "end": v(155.74, -184.5) * mm});
            skLineSegment(sketch, "E22.26.26.0", {"start": v(147.76, -177.13) * mm, "end": v(155.74, -184.5) * mm});
            skArc(sketch, "E22.29.26.0", {"start": v(129.95, -176.16) * mm, "mid": v(139.03, -173.44) * mm, "end": v(147.76, -177.13) * mm});
            skLineSegment(sketch, "E22.1.27.0", {"start": v(0, 0) * mm, "end": v(204.68, -148.7) * mm, "construction": true});
            skArc(sketch, "E22.3.27.0", {"start": v(188.77, -110.83) * mm, "mid": v(187.02, -120.14) * mm, "end": v(191.6, -128.44) * mm});
            skLineSegment(sketch, "E22.7.27.0", {"start": v(191.6, -128.44) * mm, "end": v(199.77, -135.6) * mm});
            skArc(sketch, "E22.10.27.0", {"start": v(206.24, -146.54) * mm, "mid": v(203.87, -140.56) * mm, "end": v(199.77, -135.6) * mm});
            skArc(sketch, "E22.14.27.0", {"start": v(204.68, -148.7) * mm, "mid": v(205.46, -147.63) * mm, "end": v(206.24, -146.54) * mm});
            skArc(sketch, "E22.18.27.0", {"start": v(204.68, -148.7) * mm, "mid": v(203.9, -149.79) * mm, "end": v(203.1, -150.86) * mm});
            skArc(sketch, "E22.22.27.0", {"start": v(203.1, -150.86) * mm, "mid": v(196.68, -150.46) * mm, "end": v(190.7, -148.09) * mm});
            skLineSegment(sketch, "E22.26.27.0", {"start": v(181.36, -142.54) * mm, "end": v(190.7, -148.09) * mm});
            skArc(sketch, "E22.29.27.0", {"start": v(163.74, -145.29) * mm, "mid": v(172.06, -140.75) * mm, "end": v(181.36, -142.54) * mm});
            skLineSegment(sketch, "E22.1.28.0", {"start": v(0, 0) * mm, "end": v(231.13, -102.9) * mm, "construction": true});
            skArc(sketch, "E22.3.28.0", {"start": v(207.7, -69.16) * mm, "mid": v(207.92, -78.63) * mm, "end": v(214.12, -85.8) * mm});
            skLineSegment(sketch, "E22.7.28.0", {"start": v(214.12, -85.8) * mm, "end": v(223.6, -91.1) * mm});
            skArc(sketch, "E22.10.28.0", {"start": v(232.2, -100.46) * mm, "mid": v(228.64, -95.1) * mm, "end": v(223.6, -91.1) * mm});
            skArc(sketch, "E22.14.28.0", {"start": v(231.13, -102.9) * mm, "mid": v(231.67, -101.69) * mm, "end": v(232.2, -100.46) * mm});
            skArc(sketch, "E22.18.28.0", {"start": v(231.13, -102.9) * mm, "mid": v(230.58, -104.12) * mm, "end": v(230.03, -105.33) * mm});
            skArc(sketch, "E22.22.28.0", {"start": v(230.03, -105.33) * mm, "mid": v(223.66, -106.28) * mm, "end": v(217.32, -105.2) * mm});
            skLineSegment(sketch, "E22.26.28.0", {"start": v(207.03, -101.72) * mm, "end": v(217.32, -105.2) * mm});
            skArc(sketch, "E22.29.28.0", {"start": v(190.37, -108.07) * mm, "mid": v(197.56, -101.9) * mm, "end": v(207.03, -101.72) * mm});
            skLineSegment(sketch, "E22.1.29.0", {"start": v(0, 0) * mm, "end": v(247.47, -52.6) * mm, "construction": true});
            skArc(sketch, "E22.3.29.0", {"start": v(217.53, -24.47) * mm, "mid": v(219.72, -33.68) * mm, "end": v(227.28, -39.4) * mm});
            skLineSegment(sketch, "E22.7.29.0", {"start": v(227.28, -39.4) * mm, "end": v(237.65, -42.63) * mm});
            skArc(sketch, "E22.10.29.0", {"start": v(248.01, -50) * mm, "mid": v(243.42, -45.48) * mm, "end": v(237.65, -42.63) * mm});
            skArc(sketch, "E22.14.29.0", {"start": v(247.47, -52.6) * mm, "mid": v(247.75, -51.3) * mm, "end": v(248.01, -50) * mm});
            skArc(sketch, "E22.18.29.0", {"start": v(247.47, -52.6) * mm, "mid": v(247.2, -53.9) * mm, "end": v(246.9, -55.2) * mm});
            skArc(sketch, "E22.22.29.0", {"start": v(246.9, -55.2) * mm, "mid": v(240.87, -57.46) * mm, "end": v(234.44, -57.72) * mm});
            skLineSegment(sketch, "E22.26.29.0", {"start": v(223.66, -56.45) * mm, "end": v(234.44, -57.72) * mm});
            skArc(sketch, "E22.29.29.0", {"start": v(208.68, -66.13) * mm, "mid": v(214.43, -58.6) * mm, "end": v(223.66, -56.45) * mm});
            skArc(sketch, "E23", {"start": v(-217.86, -21.3) * mm, "mid": v(-217.7, -22.88) * mm, "end": v(-217.53, -24.47) * mm});
            skArc(sketch, "E24.trimOffspring", {"start": v(-208.68, -66.13) * mm, "mid": v(-208.19, -67.64) * mm, "end": v(-207.7, -69.16) * mm});
            skArc(sketch, "E25.trimOffspring", {"start": v(-217.53, 24.47) * mm, "mid": v(-217.7, 22.88) * mm, "end": v(-217.86, 21.3) * mm});
            skArc(sketch, "E26.trimOffspring", {"start": v(-207.7, 69.16) * mm, "mid": v(-208.19, 67.64) * mm, "end": v(-208.68, 66.13) * mm});
            skArc(sketch, "E27.trimOffspring", {"start": v(-188.77, 110.83) * mm, "mid": v(-189.58, 109.45) * mm, "end": v(-190.37, 108.07) * mm});
            skArc(sketch, "E28.trimOffspring", {"start": v(-161.6, 147.65) * mm, "mid": v(-162.68, 146.47) * mm, "end": v(-163.74, 145.29) * mm});
            skArc(sketch, "E29.trimOffspring", {"start": v(-127.38, 178.03) * mm, "mid": v(-128.67, 177.1) * mm, "end": v(-129.95, 176.16) * mm});
            skArc(sketch, "E30.trimOffspring", {"start": v(-87.58, 200.62) * mm, "mid": v(-89.04, 199.98) * mm, "end": v(-90.49, 199.32) * mm});
            skArc(sketch, "E31.trimOffspring", {"start": v(-43.95, 214.45) * mm, "mid": v(-45.51, 214.12) * mm, "end": v(-47.07, 213.78) * mm});
            skArc(sketch, "E32.trimOffspring", {"start": v(1.6, 218.9) * mm, "mid": v(0, 218.9) * mm, "end": v(-1.6, 218.9) * mm});
            skArc(sketch, "E33.trimOffspring", {"start": v(47.07, 213.78) * mm, "mid": v(45.51, 214.12) * mm, "end": v(43.95, 214.45) * mm});
            skArc(sketch, "E34.trimOffspring", {"start": v(90.49, 199.32) * mm, "mid": v(89.04, 199.98) * mm, "end": v(87.58, 200.62) * mm});
            skArc(sketch, "E35.trimOffspring", {"start": v(129.95, 176.16) * mm, "mid": v(128.67, 177.1) * mm, "end": v(127.38, 178.03) * mm});
            skArc(sketch, "E36.trimOffspring", {"start": v(163.74, 145.29) * mm, "mid": v(162.68, 146.47) * mm, "end": v(161.6, 147.65) * mm});
            skArc(sketch, "E37.trimOffspring", {"start": v(190.37, 108.07) * mm, "mid": v(189.58, 109.45) * mm, "end": v(188.77, 110.83) * mm});
            skArc(sketch, "E38.trimOffspring", {"start": v(208.68, 66.13) * mm, "mid": v(208.19, 67.64) * mm, "end": v(207.7, 69.16) * mm});
            skArc(sketch, "E39.trimOffspring", {"start": v(217.86, 21.3) * mm, "mid": v(217.7, 22.88) * mm, "end": v(217.53, 24.47) * mm});
            skArc(sketch, "E40.trimOffspring", {"start": v(217.53, -24.47) * mm, "mid": v(217.7, -22.88) * mm, "end": v(217.86, -21.3) * mm});
            skArc(sketch, "E41.trimOffspring", {"start": v(207.7, -69.16) * mm, "mid": v(208.19, -67.64) * mm, "end": v(208.68, -66.13) * mm});
            skArc(sketch, "E42.trimOffspring", {"start": v(188.77, -110.83) * mm, "mid": v(189.58, -109.45) * mm, "end": v(190.37, -108.07) * mm});
            skArc(sketch, "E43.trimOffspring", {"start": v(-190.37, -108.07) * mm, "mid": v(-189.58, -109.45) * mm, "end": v(-188.77, -110.83) * mm});
            skArc(sketch, "E44.trimOffspring", {"start": v(-163.74, -145.29) * mm, "mid": v(-162.68, -146.47) * mm, "end": v(-161.6, -147.65) * mm});
            skArc(sketch, "E45.trimOffspring", {"start": v(-129.95, -176.16) * mm, "mid": v(-128.67, -177.1) * mm, "end": v(-127.38, -178.03) * mm});
            skArc(sketch, "E46.trimOffspring", {"start": v(-90.49, -199.32) * mm, "mid": v(-89.04, -199.98) * mm, "end": v(-87.58, -200.62) * mm});
            skArc(sketch, "E47.trimOffspring", {"start": v(-47.07, -213.78) * mm, "mid": v(-45.51, -214.12) * mm, "end": v(-43.95, -214.45) * mm});
            skArc(sketch, "E48.trimOffspring", {"start": v(-1.6, -218.9) * mm, "mid": v(0, -218.9) * mm, "end": v(1.6, -218.9) * mm});
            skArc(sketch, "E49.trimOffspring", {"start": v(43.95, -214.45) * mm, "mid": v(45.51, -214.12) * mm, "end": v(47.07, -213.78) * mm});
            skArc(sketch, "E50.trimOffspring", {"start": v(87.58, -200.62) * mm, "mid": v(89.04, -199.98) * mm, "end": v(90.49, -199.32) * mm});
            skArc(sketch, "E51.trimOffspring", {"start": v(127.38, -178.03) * mm, "mid": v(128.67, -177.1) * mm, "end": v(129.95, -176.16) * mm});
            skArc(sketch, "E52.trimOffspring", {"start": v(161.6, -147.65) * mm, "mid": v(162.68, -146.47) * mm, "end": v(163.74, -145.29) * mm});
            skSolve(sketch);
        }
        {
            var Q0;
            Q0 = qSketchRegion(id + "F1", true);
            extrude(context, id + "F2", {"entities" : qUnion([Q0]), "depth" : 32 * mm});
        }
        {
            var Q0;
            Q0=qCreatedBy(makeId("Right.planeOp"),FACE);
            var sketch = newSketch(context, id + "F3", { "sketchPlane" : qUnion([Q0])});
            skLineSegment(sketch, "E53.bottom", {"start": v(232.58, 21) * mm, "end": v(253.36, 21) * mm});
            skLineSegment(sketch, "E53.top", {"start": v(232.58, 11) * mm, "end": v(253.36, 11) * mm});
            skLineSegment(sketch, "E53.left", {"start": v(228.08, 16.5) * mm, "end": v(228.08, 15.5) * mm});
            skPoint(sketch, "E54.visualSharp", {"position": v(228.08, 21) * mm});
            skArc(sketch, "E54.filletArc", {"start": v(232.58, 21) * mm, "mid": v(229.4, 19.68) * mm, "end": v(228.08, 16.5) * mm});
            skPoint(sketch, "E55.visualSharp", {"position": v(228.08, 11) * mm});
            skArc(sketch, "E55.filletArc", {"start": v(228.08, 15.5) * mm, "mid": v(229.4, 12.32) * mm, "end": v(232.58, 11) * mm});
            skLineSegment(sketch, "E56", {"start": v(0, 0) * mm, "end": v(0, 49.23) * mm});
            skLineSegment(sketch, "E57", {"start": v(253.36, 21) * mm, "end": v(253.36, 11) * mm});
            skSolve(sketch);
        }
        {
            var Q0;
            Q0 = qSketchRegion(id + "F3", true);
            var Q1;
            Q1 = qConstructionFilter(qBodyType(qCreatedBy(id + "F3" ,EDGE), BodyType.WIRE), ConstructionObject.NO);
            var Q2;
            Q2=sQuery(id+"F3.wireOp",EDGE,"E56");
            revolve(context, id + "F4", {"operationType" : NewBodyOperationType.REMOVE, "entities" : qUnion([Q0]), "surfaceEntities" : qUnion([Q1]), "axis" : qUnion([Q2]), "revolveType" : RevolveType.FULL});
        }
        {
            var Q0;
            Q0=makeQuery(id+"F2.opExtrude","CAP_EDGE",EDGE,{"disambiguationData":[OSD([sQuery(id+"F1.wireOp",EDGE,"E22.3.22.0")])],"isStart":false});
            var Q1;
            Q1=makeQuery(id+"F2.opExtrude","CAP_EDGE",EDGE,{"disambiguationData":[OSD([sQuery(id+"F1.wireOp",EDGE,"E22.3.23.0")])],"isStart":false});
            var Q2;
            Q2=makeQuery(id+"F2.opExtrude","CAP_EDGE",EDGE,{"disambiguationData":[OSD([sQuery(id+"F1.wireOp",EDGE,"E22.3.24.0")])],"isStart":false});
            var Q3;
            Q3=makeQuery(id+"F2.opExtrude","CAP_EDGE",EDGE,{"disambiguationData":[OSD([sQuery(id+"F1.wireOp",EDGE,"E22.3.25.0")])],"isStart":false});
            var Q4;
            Q4=makeQuery(id+"F2.opExtrude","CAP_EDGE",EDGE,{"disambiguationData":[OSD([sQuery(id+"F1.wireOp",EDGE,"E22.3.26.0")])],"isStart":false});
            var Q5;
            Q5=makeQuery(id+"F2.opExtrude","CAP_EDGE",EDGE,{"disambiguationData":[OSD([sQuery(id+"F1.wireOp",EDGE,"E22.14.23.0"),sQuery(id+"F1.wireOp",EDGE,"E22.18.23.0")])],"isStart":false});
            var Q6;
            Q6=makeQuery(id+"F2.opExtrude","CAP_EDGE",EDGE,{"disambiguationData":[OSD([sQuery(id+"F1.wireOp",EDGE,"E22.14.24.0"),sQuery(id+"F1.wireOp",EDGE,"E22.18.24.0")])],"isStart":false});
            var Q7;
            Q7=makeQuery(id+"F2.opExtrude","CAP_EDGE",EDGE,{"disambiguationData":[OSD([sQuery(id+"F1.wireOp",EDGE,"E22.14.25.0"),sQuery(id+"F1.wireOp",EDGE,"E22.18.25.0")])],"isStart":false});
            var Q8;
            Q8=makeQuery(id+"F2.opExtrude","CAP_EDGE",EDGE,{"disambiguationData":[OSD([sQuery(id+"F1.wireOp",EDGE,"E22.14.26.0"),sQuery(id+"F1.wireOp",EDGE,"E22.18.26.0")])],"isStart":false});
            var Q9;
            Q9=makeQuery(id+"F2.opExtrude","CAP_EDGE",EDGE,{"disambiguationData":[OSD([sQuery(id+"F1.wireOp",EDGE,"E22.3.27.0")])],"isStart":false});
            var Q10;
            Q10=makeQuery(id+"F2.opExtrude","CAP_EDGE",EDGE,{"disambiguationData":[OSD([sQuery(id+"F1.wireOp",EDGE,"E22.14.27.0"),sQuery(id+"F1.wireOp",EDGE,"E22.18.27.0")])],"isStart":false});
            var Q11;
            Q11=makeQuery(id+"F2.opExtrude","CAP_EDGE",EDGE,{"disambiguationData":[OSD([sQuery(id+"F1.wireOp",EDGE,"E22.14.28.0"),sQuery(id+"F1.wireOp",EDGE,"E22.18.28.0")])],"isStart":false});
            var Q12;
            Q12=makeQuery(id+"F2.opExtrude","CAP_EDGE",EDGE,{"disambiguationData":[OSD([sQuery(id+"F1.wireOp",EDGE,"E22.10.28.0")])],"isStart":false});
            var Q13;
            Q13=makeQuery(id+"F2.opExtrude","CAP_EDGE",EDGE,{"disambiguationData":[OSD([sQuery(id+"F1.wireOp",EDGE,"E22.14.29.0"),sQuery(id+"F1.wireOp",EDGE,"E22.18.29.0")])],"isStart":false});
            var Q14;
            Q14=makeQuery(id+"F2.opExtrude","CAP_EDGE",EDGE,{"disambiguationData":[OSD([sQuery(id+"F1.wireOp",EDGE,"E22.10.29.0")])],"isStart":false});
            var Q15;
            Q15=makeQuery(id+"F2.opExtrude","CAP_EDGE",EDGE,{"disambiguationData":[OSD([sQuery(id+"F1.wireOp",EDGE,"E22.3.29.0")])],"isStart":false});
            var Q16;
            Q16=makeQuery(id+"F2.opExtrude","CAP_EDGE",EDGE,{"disambiguationData":[OSD([sQuery(id+"F1.wireOp",EDGE,"E11.0")])],"isStart":false});
            var Q17;
            Q17=makeQuery(id+"F2.opExtrude","CAP_EDGE",EDGE,{"disambiguationData":[OSD([sQuery(id+"F1.wireOp",EDGE,"E20.1.1")])],"isStart":false});
            var Q18;
            Q18=makeQuery(id+"F2.opExtrude","CAP_EDGE",EDGE,{"disambiguationData":[OSD([sQuery(id+"F1.wireOp",EDGE,"E13.0"),sQuery(id+"F1.wireOp",EDGE,"E16.MirrorCS")])],"isStart":false});
            var Q19;
            Q19=makeQuery(id+"F2.opExtrude","CAP_EDGE",EDGE,{"disambiguationData":[OSD([sQuery(id+"F1.wireOp",EDGE,"E20.1.4"),sQuery(id+"F1.wireOp",EDGE,"E20.1.5")])],"isStart":false});
            var Q20;
            Q20=makeQuery(id+"F2.opExtrude","CAP_EDGE",EDGE,{"disambiguationData":[OSD([sQuery(id+"F1.wireOp",EDGE,"E20.2.4"),sQuery(id+"F1.wireOp",EDGE,"E20.2.5")])],"isStart":false});
            var Q21;
            Q21=makeQuery(id+"F2.opExtrude","CAP_EDGE",EDGE,{"disambiguationData":[OSD([sQuery(id+"F1.wireOp",EDGE,"E20.2.1")])],"isStart":false});
            var Q22;
            Q22=makeQuery(id+"F2.opExtrude","CAP_EDGE",EDGE,{"disambiguationData":[OSD([sQuery(id+"F1.wireOp",EDGE,"E21.14.3.0"),sQuery(id+"F1.wireOp",EDGE,"E21.18.3.0")])],"isStart":false});
            var Q23;
            Q23=makeQuery(id+"F2.opExtrude","CAP_EDGE",EDGE,{"disambiguationData":[OSD([sQuery(id+"F1.wireOp",EDGE,"E21.3.3.0")])],"isStart":false});
            var Q24;
            Q24=makeQuery(id+"F2.opExtrude","CAP_EDGE",EDGE,{"disambiguationData":[OSD([sQuery(id+"F1.wireOp",EDGE,"E21.14.4.0"),sQuery(id+"F1.wireOp",EDGE,"E21.18.4.0")])],"isStart":false});
            var Q25;
            Q25=makeQuery(id+"F2.opExtrude","CAP_EDGE",EDGE,{"disambiguationData":[OSD([sQuery(id+"F1.wireOp",EDGE,"E21.3.4.0")])],"isStart":false});
            var Q26;
            Q26=makeQuery(id+"F2.opExtrude","CAP_EDGE",EDGE,{"disambiguationData":[OSD([sQuery(id+"F1.wireOp",EDGE,"E21.14.5.0"),sQuery(id+"F1.wireOp",EDGE,"E21.18.5.0")])],"isStart":false});
            var Q27;
            Q27=makeQuery(id+"F2.opExtrude","CAP_EDGE",EDGE,{"disambiguationData":[OSD([sQuery(id+"F1.wireOp",EDGE,"E21.3.5.0")])],"isStart":false});
            var Q28;
            Q28=makeQuery(id+"F2.opExtrude","CAP_EDGE",EDGE,{"disambiguationData":[OSD([sQuery(id+"F1.wireOp",EDGE,"E22.14.6.0"),sQuery(id+"F1.wireOp",EDGE,"E22.18.6.0")])],"isStart":false});
            var Q29;
            Q29=makeQuery(id+"F2.opExtrude","CAP_EDGE",EDGE,{"disambiguationData":[OSD([sQuery(id+"F1.wireOp",EDGE,"E22.3.6.0")])],"isStart":false});
            var Q30;
            Q30=makeQuery(id+"F2.opExtrude","CAP_EDGE",EDGE,{"disambiguationData":[OSD([sQuery(id+"F1.wireOp",EDGE,"E22.14.7.0"),sQuery(id+"F1.wireOp",EDGE,"E22.18.7.0")])],"isStart":false});
            var Q31;
            Q31=makeQuery(id+"F2.opExtrude","CAP_EDGE",EDGE,{"disambiguationData":[OSD([sQuery(id+"F1.wireOp",EDGE,"E22.3.7.0")])],"isStart":false});
            var Q32;
            Q32=makeQuery(id+"F2.opExtrude","CAP_EDGE",EDGE,{"disambiguationData":[OSD([sQuery(id+"F1.wireOp",EDGE,"E22.14.8.0"),sQuery(id+"F1.wireOp",EDGE,"E22.18.8.0")])],"isStart":false});
            var Q33;
            Q33=makeQuery(id+"F2.opExtrude","CAP_EDGE",EDGE,{"disambiguationData":[OSD([sQuery(id+"F1.wireOp",EDGE,"E22.3.8.0")])],"isStart":false});
            var Q34;
            Q34=makeQuery(id+"F2.opExtrude","CAP_EDGE",EDGE,{"disambiguationData":[OSD([sQuery(id+"F1.wireOp",EDGE,"E22.14.9.0"),sQuery(id+"F1.wireOp",EDGE,"E22.18.9.0")])],"isStart":false});
            var Q35;
            Q35=makeQuery(id+"F2.opExtrude","CAP_EDGE",EDGE,{"disambiguationData":[OSD([sQuery(id+"F1.wireOp",EDGE,"E22.3.9.0")])],"isStart":false});
            var Q36;
            Q36=makeQuery(id+"F2.opExtrude","CAP_EDGE",EDGE,{"disambiguationData":[OSD([sQuery(id+"F1.wireOp",EDGE,"E22.14.10.0"),sQuery(id+"F1.wireOp",EDGE,"E22.18.10.0")])],"isStart":false});
            var Q37;
            Q37=makeQuery(id+"F2.opExtrude","CAP_EDGE",EDGE,{"disambiguationData":[OSD([sQuery(id+"F1.wireOp",EDGE,"E22.3.10.0")])],"isStart":false});
            var Q38;
            Q38=makeQuery(id+"F2.opExtrude","CAP_EDGE",EDGE,{"disambiguationData":[OSD([sQuery(id+"F1.wireOp",EDGE,"E22.3.11.0")])],"isStart":false});
            var Q39;
            Q39=makeQuery(id+"F2.opExtrude","CAP_EDGE",EDGE,{"disambiguationData":[OSD([sQuery(id+"F1.wireOp",EDGE,"E22.14.12.0"),sQuery(id+"F1.wireOp",EDGE,"E22.18.12.0")])],"isStart":false});
            var Q40;
            Q40=makeQuery(id+"F2.opExtrude","CAP_EDGE",EDGE,{"disambiguationData":[OSD([sQuery(id+"F1.wireOp",EDGE,"E22.3.12.0")])],"isStart":false});
            var Q41;
            Q41=makeQuery(id+"F2.opExtrude","CAP_EDGE",EDGE,{"disambiguationData":[OSD([sQuery(id+"F1.wireOp",EDGE,"E22.14.13.0"),sQuery(id+"F1.wireOp",EDGE,"E22.18.13.0")])],"isStart":false});
            var Q42;
            Q42=makeQuery(id+"F2.opExtrude","CAP_EDGE",EDGE,{"disambiguationData":[OSD([sQuery(id+"F1.wireOp",EDGE,"E22.3.13.0")])],"isStart":false});
            var Q43;
            Q43=makeQuery(id+"F2.opExtrude","CAP_EDGE",EDGE,{"disambiguationData":[OSD([sQuery(id+"F1.wireOp",EDGE,"E22.14.14.0"),sQuery(id+"F1.wireOp",EDGE,"E22.18.14.0")])],"isStart":false});
            var Q44;
            Q44=makeQuery(id+"F2.opExtrude","CAP_EDGE",EDGE,{"disambiguationData":[OSD([sQuery(id+"F1.wireOp",EDGE,"E22.3.14.0")])],"isStart":false});
            var Q45;
            Q45=makeQuery(id+"F2.opExtrude","CAP_EDGE",EDGE,{"disambiguationData":[OSD([sQuery(id+"F1.wireOp",EDGE,"E22.14.15.0"),sQuery(id+"F1.wireOp",EDGE,"E22.18.15.0")])],"isStart":false});
            var Q46;
            Q46=makeQuery(id+"F2.opExtrude","CAP_EDGE",EDGE,{"disambiguationData":[OSD([sQuery(id+"F1.wireOp",EDGE,"E22.3.15.0")])],"isStart":false});
            var Q47;
            Q47=makeQuery(id+"F2.opExtrude","CAP_EDGE",EDGE,{"disambiguationData":[OSD([sQuery(id+"F1.wireOp",EDGE,"E22.14.16.0"),sQuery(id+"F1.wireOp",EDGE,"E22.18.16.0")])],"isStart":false});
            var Q48;
            Q48=makeQuery(id+"F2.opExtrude","CAP_EDGE",EDGE,{"disambiguationData":[OSD([sQuery(id+"F1.wireOp",EDGE,"E22.3.16.0")])],"isStart":false});
            var Q49;
            Q49=makeQuery(id+"F2.opExtrude","CAP_EDGE",EDGE,{"disambiguationData":[OSD([sQuery(id+"F1.wireOp",EDGE,"E22.14.17.0"),sQuery(id+"F1.wireOp",EDGE,"E22.18.17.0")])],"isStart":false});
            var Q50;
            Q50=makeQuery(id+"F2.opExtrude","CAP_EDGE",EDGE,{"disambiguationData":[OSD([sQuery(id+"F1.wireOp",EDGE,"E22.3.17.0")])],"isStart":false});
            var Q51;
            Q51=makeQuery(id+"F2.opExtrude","CAP_EDGE",EDGE,{"disambiguationData":[OSD([sQuery(id+"F1.wireOp",EDGE,"E22.14.18.0"),sQuery(id+"F1.wireOp",EDGE,"E22.18.18.0")])],"isStart":false});
            var Q52;
            Q52=makeQuery(id+"F2.opExtrude","CAP_EDGE",EDGE,{"disambiguationData":[OSD([sQuery(id+"F1.wireOp",EDGE,"E22.3.18.0")])],"isStart":false});
            var Q53;
            Q53=makeQuery(id+"F2.opExtrude","CAP_EDGE",EDGE,{"disambiguationData":[OSD([sQuery(id+"F1.wireOp",EDGE,"E22.14.19.0"),sQuery(id+"F1.wireOp",EDGE,"E22.18.19.0")])],"isStart":false});
            var Q54;
            Q54=makeQuery(id+"F2.opExtrude","CAP_EDGE",EDGE,{"disambiguationData":[OSD([sQuery(id+"F1.wireOp",EDGE,"E22.3.19.0")])],"isStart":false});
            var Q55;
            Q55=makeQuery(id+"F2.opExtrude","CAP_EDGE",EDGE,{"disambiguationData":[OSD([sQuery(id+"F1.wireOp",EDGE,"E22.14.20.0"),sQuery(id+"F1.wireOp",EDGE,"E22.18.20.0")])],"isStart":false});
            var Q56;
            Q56=makeQuery(id+"F2.opExtrude","CAP_EDGE",EDGE,{"disambiguationData":[OSD([sQuery(id+"F1.wireOp",EDGE,"E22.3.20.0")])],"isStart":false});
            var Q57;
            Q57=makeQuery(id+"F2.opExtrude","CAP_EDGE",EDGE,{"disambiguationData":[OSD([sQuery(id+"F1.wireOp",EDGE,"E22.14.21.0"),sQuery(id+"F1.wireOp",EDGE,"E22.18.21.0")])],"isStart":false});
            var Q58;
            Q58=makeQuery(id+"F2.opExtrude","CAP_EDGE",EDGE,{"disambiguationData":[OSD([sQuery(id+"F1.wireOp",EDGE,"E22.3.21.0")])],"isStart":false});
            var Q59;
            Q59=makeQuery(id+"F2.opExtrude","CAP_EDGE",EDGE,{"disambiguationData":[OSD([sQuery(id+"F1.wireOp",EDGE,"E22.14.22.0"),sQuery(id+"F1.wireOp",EDGE,"E22.18.22.0")])],"isStart":false});
            var Q60;
            Q60=makeQuery(id+"F2.opExtrude","CAP_EDGE",EDGE,{"disambiguationData":[OSD([sQuery(id+"F1.wireOp",EDGE,"E22.14.10.0"),sQuery(id+"F1.wireOp",EDGE,"E22.18.10.0")])],"isStart":true});
            var Q61;
            Q61=makeQuery(id+"F2.opExtrude","CAP_EDGE",EDGE,{"disambiguationData":[OSD([sQuery(id+"F1.wireOp",EDGE,"E22.29.10.0")])],"isStart":true});
            var Q62;
            Q62=makeQuery(id+"F2.opExtrude","CAP_EDGE",EDGE,{"disambiguationData":[OSD([sQuery(id+"F1.wireOp",EDGE,"E22.14.9.0"),sQuery(id+"F1.wireOp",EDGE,"E22.18.9.0")])],"isStart":true});
            var Q63;
            Q63=makeQuery(id+"F2.opExtrude","CAP_EDGE",EDGE,{"disambiguationData":[OSD([sQuery(id+"F1.wireOp",EDGE,"E22.29.9.0")])],"isStart":true});
            var Q64;
            Q64=makeQuery(id+"F2.opExtrude","CAP_EDGE",EDGE,{"disambiguationData":[OSD([sQuery(id+"F1.wireOp",EDGE,"E22.14.8.0"),sQuery(id+"F1.wireOp",EDGE,"E22.18.8.0")])],"isStart":true});
            var Q65;
            Q65=makeQuery(id+"F2.opExtrude","CAP_EDGE",EDGE,{"disambiguationData":[OSD([sQuery(id+"F1.wireOp",EDGE,"E22.29.8.0")])],"isStart":true});
            var Q66;
            Q66=makeQuery(id+"F2.opExtrude","CAP_EDGE",EDGE,{"disambiguationData":[OSD([sQuery(id+"F1.wireOp",EDGE,"E22.14.7.0"),sQuery(id+"F1.wireOp",EDGE,"E22.18.7.0")])],"isStart":true});
            var Q67;
            Q67=makeQuery(id+"F2.opExtrude","CAP_EDGE",EDGE,{"disambiguationData":[OSD([sQuery(id+"F1.wireOp",EDGE,"E22.29.7.0")])],"isStart":true});
            var Q68;
            Q68=makeQuery(id+"F2.opExtrude","CAP_EDGE",EDGE,{"disambiguationData":[OSD([sQuery(id+"F1.wireOp",EDGE,"E22.14.6.0"),sQuery(id+"F1.wireOp",EDGE,"E22.18.6.0")])],"isStart":true});
            var Q69;
            Q69=makeQuery(id+"F2.opExtrude","CAP_EDGE",EDGE,{"disambiguationData":[OSD([sQuery(id+"F1.wireOp",EDGE,"E22.29.6.0")])],"isStart":true});
            var Q70;
            Q70=makeQuery(id+"F2.opExtrude","CAP_EDGE",EDGE,{"disambiguationData":[OSD([sQuery(id+"F1.wireOp",EDGE,"E21.14.5.0"),sQuery(id+"F1.wireOp",EDGE,"E21.18.5.0")])],"isStart":true});
            var Q71;
            Q71=makeQuery(id+"F2.opExtrude","CAP_EDGE",EDGE,{"disambiguationData":[OSD([sQuery(id+"F1.wireOp",EDGE,"E21.29.5.0")])],"isStart":true});
            var Q72;
            Q72=makeQuery(id+"F2.opExtrude","CAP_EDGE",EDGE,{"disambiguationData":[OSD([sQuery(id+"F1.wireOp",EDGE,"E21.14.4.0"),sQuery(id+"F1.wireOp",EDGE,"E21.18.4.0")])],"isStart":true});
            var Q73;
            Q73=makeQuery(id+"F2.opExtrude","CAP_EDGE",EDGE,{"disambiguationData":[OSD([sQuery(id+"F1.wireOp",EDGE,"E21.29.4.0")])],"isStart":true});
            var Q74;
            Q74=makeQuery(id+"F2.opExtrude","CAP_EDGE",EDGE,{"disambiguationData":[OSD([sQuery(id+"F1.wireOp",EDGE,"E21.14.3.0"),sQuery(id+"F1.wireOp",EDGE,"E21.18.3.0")])],"isStart":true});
            var Q75;
            Q75=makeQuery(id+"F2.opExtrude","CAP_EDGE",EDGE,{"disambiguationData":[OSD([sQuery(id+"F1.wireOp",EDGE,"E21.29.3.0")])],"isStart":true});
            var Q76;
            Q76=makeQuery(id+"F2.opExtrude","CAP_EDGE",EDGE,{"disambiguationData":[OSD([sQuery(id+"F1.wireOp",EDGE,"E20.2.4"),sQuery(id+"F1.wireOp",EDGE,"E20.2.5")])],"isStart":true});
            var Q77;
            Q77=makeQuery(id+"F2.opExtrude","CAP_EDGE",EDGE,{"disambiguationData":[OSD([sQuery(id+"F1.wireOp",EDGE,"E20.2.8")])],"isStart":true});
            var Q78;
            Q78=makeQuery(id+"F2.opExtrude","CAP_EDGE",EDGE,{"disambiguationData":[OSD([sQuery(id+"F1.wireOp",EDGE,"E20.1.4"),sQuery(id+"F1.wireOp",EDGE,"E20.1.5")])],"isStart":true});
            var Q79;
            Q79=makeQuery(id+"F2.opExtrude","CAP_EDGE",EDGE,{"disambiguationData":[OSD([sQuery(id+"F1.wireOp",EDGE,"E20.1.8")])],"isStart":true});
            var Q80;
            Q80=makeQuery(id+"F2.opExtrude","CAP_EDGE",EDGE,{"disambiguationData":[OSD([sQuery(id+"F1.wireOp",EDGE,"E13.0"),sQuery(id+"F1.wireOp",EDGE,"E16.MirrorCS")])],"isStart":true});
            var Q81;
            Q81=makeQuery(id+"F2.opExtrude","CAP_EDGE",EDGE,{"disambiguationData":[OSD([sQuery(id+"F1.wireOp",EDGE,"E19.MirrorCS")])],"isStart":true});
            var Q82;
            Q82=makeQuery(id+"F2.opExtrude","CAP_EDGE",EDGE,{"disambiguationData":[OSD([sQuery(id+"F1.wireOp",EDGE,"E22.14.29.0"),sQuery(id+"F1.wireOp",EDGE,"E22.18.29.0")])],"isStart":true});
            var Q83;
            Q83=makeQuery(id+"F2.opExtrude","CAP_EDGE",EDGE,{"disambiguationData":[OSD([sQuery(id+"F1.wireOp",EDGE,"E22.29.29.0")])],"isStart":true});
            var Q84;
            Q84=makeQuery(id+"F2.opExtrude","CAP_EDGE",EDGE,{"disambiguationData":[OSD([sQuery(id+"F1.wireOp",EDGE,"E22.14.28.0"),sQuery(id+"F1.wireOp",EDGE,"E22.18.28.0")])],"isStart":true});
            var Q85;
            Q85=makeQuery(id+"F2.opExtrude","CAP_EDGE",EDGE,{"disambiguationData":[OSD([sQuery(id+"F1.wireOp",EDGE,"E22.29.28.0")])],"isStart":true});
            var Q86;
            Q86=makeQuery(id+"F2.opExtrude","CAP_EDGE",EDGE,{"disambiguationData":[OSD([sQuery(id+"F1.wireOp",EDGE,"E22.14.27.0"),sQuery(id+"F1.wireOp",EDGE,"E22.18.27.0")])],"isStart":true});
            var Q87;
            Q87=makeQuery(id+"F2.opExtrude","CAP_EDGE",EDGE,{"disambiguationData":[OSD([sQuery(id+"F1.wireOp",EDGE,"E22.29.27.0")])],"isStart":true});
            var Q88;
            Q88=makeQuery(id+"F2.opExtrude","CAP_EDGE",EDGE,{"disambiguationData":[OSD([sQuery(id+"F1.wireOp",EDGE,"E22.29.26.0")])],"isStart":true});
            var Q89;
            Q89=makeQuery(id+"F2.opExtrude","CAP_EDGE",EDGE,{"disambiguationData":[OSD([sQuery(id+"F1.wireOp",EDGE,"E22.14.26.0"),sQuery(id+"F1.wireOp",EDGE,"E22.18.26.0")])],"isStart":true});
            var Q90;
            Q90=makeQuery(id+"F2.opExtrude","CAP_EDGE",EDGE,{"disambiguationData":[OSD([sQuery(id+"F1.wireOp",EDGE,"E22.14.25.0"),sQuery(id+"F1.wireOp",EDGE,"E22.18.25.0")])],"isStart":true});
            var Q91;
            Q91=makeQuery(id+"F2.opExtrude","CAP_EDGE",EDGE,{"disambiguationData":[OSD([sQuery(id+"F1.wireOp",EDGE,"E22.29.25.0")])],"isStart":true});
            var Q92;
            Q92=makeQuery(id+"F2.opExtrude","CAP_EDGE",EDGE,{"disambiguationData":[OSD([sQuery(id+"F1.wireOp",EDGE,"E22.14.24.0"),sQuery(id+"F1.wireOp",EDGE,"E22.18.24.0")])],"isStart":true});
            var Q93;
            Q93=makeQuery(id+"F2.opExtrude","CAP_EDGE",EDGE,{"disambiguationData":[OSD([sQuery(id+"F1.wireOp",EDGE,"E22.29.24.0")])],"isStart":true});
            var Q94;
            Q94=makeQuery(id+"F2.opExtrude","CAP_EDGE",EDGE,{"disambiguationData":[OSD([sQuery(id+"F1.wireOp",EDGE,"E22.14.23.0"),sQuery(id+"F1.wireOp",EDGE,"E22.18.23.0")])],"isStart":true});
            var Q95;
            Q95=makeQuery(id+"F2.opExtrude","CAP_EDGE",EDGE,{"disambiguationData":[OSD([sQuery(id+"F1.wireOp",EDGE,"E22.29.23.0")])],"isStart":true});
            var Q96;
            Q96=makeQuery(id+"F2.opExtrude","CAP_EDGE",EDGE,{"disambiguationData":[OSD([sQuery(id+"F1.wireOp",EDGE,"E22.14.22.0"),sQuery(id+"F1.wireOp",EDGE,"E22.18.22.0")])],"isStart":true});
            var Q97;
            Q97=makeQuery(id+"F2.opExtrude","CAP_EDGE",EDGE,{"disambiguationData":[OSD([sQuery(id+"F1.wireOp",EDGE,"E22.14.21.0"),sQuery(id+"F1.wireOp",EDGE,"E22.18.21.0")])],"isStart":true});
            var Q98;
            Q98=makeQuery(id+"F2.opExtrude","CAP_EDGE",EDGE,{"disambiguationData":[OSD([sQuery(id+"F1.wireOp",EDGE,"E22.29.21.0")])],"isStart":true});
            var Q99;
            Q99=makeQuery(id+"F2.opExtrude","CAP_EDGE",EDGE,{"disambiguationData":[OSD([sQuery(id+"F1.wireOp",EDGE,"E22.14.20.0"),sQuery(id+"F1.wireOp",EDGE,"E22.18.20.0")])],"isStart":true});
            var Q100;
            Q100=makeQuery(id+"F2.opExtrude","CAP_EDGE",EDGE,{"disambiguationData":[OSD([sQuery(id+"F1.wireOp",EDGE,"E22.29.20.0")])],"isStart":true});
            var Q101;
            Q101=makeQuery(id+"F2.opExtrude","CAP_EDGE",EDGE,{"disambiguationData":[OSD([sQuery(id+"F1.wireOp",EDGE,"E22.14.19.0"),sQuery(id+"F1.wireOp",EDGE,"E22.18.19.0")])],"isStart":true});
            var Q102;
            Q102=makeQuery(id+"F2.opExtrude","CAP_EDGE",EDGE,{"disambiguationData":[OSD([sQuery(id+"F1.wireOp",EDGE,"E22.29.19.0")])],"isStart":true});
            var Q103;
            Q103=makeQuery(id+"F2.opExtrude","CAP_EDGE",EDGE,{"disambiguationData":[OSD([sQuery(id+"F1.wireOp",EDGE,"E22.14.18.0"),sQuery(id+"F1.wireOp",EDGE,"E22.18.18.0")])],"isStart":true});
            var Q104;
            Q104=makeQuery(id+"F2.opExtrude","CAP_EDGE",EDGE,{"disambiguationData":[OSD([sQuery(id+"F1.wireOp",EDGE,"E22.29.18.0")])],"isStart":true});
            var Q105;
            Q105=makeQuery(id+"F2.opExtrude","CAP_EDGE",EDGE,{"disambiguationData":[OSD([sQuery(id+"F1.wireOp",EDGE,"E22.14.17.0"),sQuery(id+"F1.wireOp",EDGE,"E22.18.17.0")])],"isStart":true});
            var Q106;
            Q106=makeQuery(id+"F2.opExtrude","CAP_EDGE",EDGE,{"disambiguationData":[OSD([sQuery(id+"F1.wireOp",EDGE,"E22.29.17.0")])],"isStart":true});
            var Q107;
            Q107=makeQuery(id+"F2.opExtrude","CAP_EDGE",EDGE,{"disambiguationData":[OSD([sQuery(id+"F1.wireOp",EDGE,"E22.14.16.0"),sQuery(id+"F1.wireOp",EDGE,"E22.18.16.0")])],"isStart":true});
            var Q108;
            Q108=makeQuery(id+"F2.opExtrude","CAP_EDGE",EDGE,{"disambiguationData":[OSD([sQuery(id+"F1.wireOp",EDGE,"E22.29.16.0")])],"isStart":true});
            var Q109;
            Q109=makeQuery(id+"F2.opExtrude","CAP_EDGE",EDGE,{"disambiguationData":[OSD([sQuery(id+"F1.wireOp",EDGE,"E22.14.15.0"),sQuery(id+"F1.wireOp",EDGE,"E22.18.15.0")])],"isStart":true});
            var Q110;
            Q110=makeQuery(id+"F2.opExtrude","CAP_EDGE",EDGE,{"disambiguationData":[OSD([sQuery(id+"F1.wireOp",EDGE,"E22.29.15.0")])],"isStart":true});
            var Q111;
            Q111=makeQuery(id+"F2.opExtrude","CAP_EDGE",EDGE,{"disambiguationData":[OSD([sQuery(id+"F1.wireOp",EDGE,"E22.14.14.0"),sQuery(id+"F1.wireOp",EDGE,"E22.18.14.0")])],"isStart":true});
            var Q112;
            Q112=makeQuery(id+"F2.opExtrude","CAP_EDGE",EDGE,{"disambiguationData":[OSD([sQuery(id+"F1.wireOp",EDGE,"E22.29.14.0")])],"isStart":true});
            var Q113;
            Q113=makeQuery(id+"F2.opExtrude","CAP_EDGE",EDGE,{"disambiguationData":[OSD([sQuery(id+"F1.wireOp",EDGE,"E22.14.13.0"),sQuery(id+"F1.wireOp",EDGE,"E22.18.13.0")])],"isStart":true});
            var Q114;
            Q114=makeQuery(id+"F2.opExtrude","CAP_EDGE",EDGE,{"disambiguationData":[OSD([sQuery(id+"F1.wireOp",EDGE,"E22.29.13.0")])],"isStart":true});
            var Q115;
            Q115=makeQuery(id+"F2.opExtrude","CAP_EDGE",EDGE,{"disambiguationData":[OSD([sQuery(id+"F1.wireOp",EDGE,"E22.14.12.0"),sQuery(id+"F1.wireOp",EDGE,"E22.18.12.0")])],"isStart":true});
            var Q116;
            Q116=makeQuery(id+"F2.opExtrude","CAP_EDGE",EDGE,{"disambiguationData":[OSD([sQuery(id+"F1.wireOp",EDGE,"E22.29.12.0")])],"isStart":true});
            var Q117;
            Q117=makeQuery(id+"F2.opExtrude","CAP_EDGE",EDGE,{"disambiguationData":[OSD([sQuery(id+"F1.wireOp",EDGE,"E22.14.11.0"),sQuery(id+"F1.wireOp",EDGE,"E22.18.11.0")])],"isStart":true});
            var Q118;
            Q118=makeQuery(id+"F2.opExtrude","CAP_EDGE",EDGE,{"disambiguationData":[OSD([sQuery(id+"F1.wireOp",EDGE,"E22.29.11.0")])],"isStart":true});
            var Q119;
            Q119=makeQuery(id+"F2.opExtrude","CAP_EDGE",EDGE,{"disambiguationData":[OSD([sQuery(id+"F1.wireOp",EDGE,"E22.3.10.0")])],"isStart":true});
            chamfer(context, id + "F5", {"entities" : qUnion([Q0, Q1, Q2, Q3, Q4, Q5, Q6, Q7, Q8, Q9, Q10, Q11, Q12, Q13, Q14, Q15, Q16, Q17, Q18, Q19, Q20, Q21, Q22, Q23, Q24, Q25, Q26, Q27, Q28, Q29, Q30, Q31, Q32, Q33, Q34, Q35, Q36, Q37, Q38, Q39, Q40, Q41, Q42, Q43, Q44, Q45, Q46, Q47, Q48, Q49, Q50, Q51, Q52, Q53, Q54, Q55, Q56, Q57, Q58, Q59, Q60, Q61, Q62, Q63, Q64, Q65, Q66, Q67, Q68, Q69, Q70, Q71, Q72, Q73, Q74, Q75, Q76, Q77, Q78, Q79, Q80, Q81, Q82, Q83, Q84, Q85, Q86, Q87, Q88, Q89, Q90, Q91, Q92, Q93, Q94, Q95, Q96, Q97, Q98, Q99, Q100, Q101, Q102, Q103, Q104, Q105, Q106, Q107, Q108, Q109, Q110, Q111, Q112, Q113, Q114, Q115, Q116, Q117, Q118, Q119]), "chamferType" : ChamferType.OFFSET_ANGLE, "width" : 2 * mm, "oppositeDirection" : false, "angle" : 45 * degree, "tangentPropagation" : true});
        }
        {
            var Q0;
            Q0=qCreatedBy(makeId("Top.planeOp"),FACE);
            var sketch = newSketch(context, id + "F6", { "sketchPlane" : qUnion([Q0])});
            skCircle(sketch, "E58", {"center": v(0, 0) * mm, "radius": 45 * mm});
            skSolve(sketch);
        }
        {
            var Q0;
            Q0 = qSketchRegion(id + "F6", true);
            extrude(context, id + "F7", {"entities" : qUnion([Q0]), "operationType" : NewBodyOperationType.REMOVE, "oppositeDirection" : true, "depth" : 50 * mm, "hasSecondDirection" : true, "secondDirectionOppositeDirection" : false, "secondDirectionDepth" : 69.89 * mm});
        }
        {
            var Q0;
            Q0=makeQuery(id+"F7.boolean.opBoolean","INTERSECT",EDGE,{"derivedFrom":[makeQuery(id+"F2.opExtrude","CAP_FACE",FACE,{"disambiguationData":[OSD([sQuery(id+"F1.wireOp",EDGE,"E11.0"),sQuery(id+"F1.wireOp",EDGE,"E12.0"),sQuery(id+"F1.wireOp",EDGE,"E13.0"),sQuery(id+"F1.wireOp",EDGE,"E15.0"),sQuery(id+"F1.wireOp",EDGE,"E16.MirrorCS"),sQuery(id+"F1.wireOp",EDGE,"E17.MirrorCS"),sQuery(id+"F1.wireOp",EDGE,"E18.MirrorCS"),sQuery(id+"F1.wireOp",EDGE,"E19.MirrorCS"),sQuery(id+"F1.wireOp",EDGE,"E20.1.1"),sQuery(id+"F1.wireOp",EDGE,"E20.1.2"),sQuery(id+"F1.wireOp",EDGE,"E20.1.3"),sQuery(id+"F1.wireOp",EDGE,"E20.1.4"),sQuery(id+"F1.wireOp",EDGE,"E20.1.5"),sQuery(id+"F1.wireOp",EDGE,"E20.1.6"),sQuery(id+"F1.wireOp",EDGE,"E20.1.7"),sQuery(id+"F1.wireOp",EDGE,"E20.1.8"),sQuery(id+"F1.wireOp",EDGE,"E20.2.1"),sQuery(id+"F1.wireOp",EDGE,"E20.2.2"),sQuery(id+"F1.wireOp",EDGE,"E20.2.3"),sQuery(id+"F1.wireOp",EDGE,"E20.2.4"),sQuery(id+"F1.wireOp",EDGE,"E20.2.5"),sQuery(id+"F1.wireOp",EDGE,"E20.2.6"),sQuery(id+"F1.wireOp",EDGE,"E20.2.7"),sQuery(id+"F1.wireOp",EDGE,"E20.2.8"),sQuery(id+"F1.wireOp",EDGE,"E21.3.3.0"),sQuery(id+"F1.wireOp",EDGE,"E21.7.3.0"),sQuery(id+"F1.wireOp",EDGE,"E21.10.3.0"),sQuery(id+"F1.wireOp",EDGE,"E21.14.3.0"),sQuery(id+"F1.wireOp",EDGE,"E21.18.3.0"),sQuery(id+"F1.wireOp",EDGE,"E21.22.3.0"),sQuery(id+"F1.wireOp",EDGE,"E21.26.3.0"),sQuery(id+"F1.wireOp",EDGE,"E21.29.3.0"),sQuery(id+"F1.wireOp",EDGE,"E21.3.4.0"),sQuery(id+"F1.wireOp",EDGE,"E21.7.4.0"),sQuery(id+"F1.wireOp",EDGE,"E21.10.4.0"),sQuery(id+"F1.wireOp",EDGE,"E21.14.4.0"),sQuery(id+"F1.wireOp",EDGE,"E21.18.4.0"),sQuery(id+"F1.wireOp",EDGE,"E21.22.4.0"),sQuery(id+"F1.wireOp",EDGE,"E21.26.4.0"),sQuery(id+"F1.wireOp",EDGE,"E21.29.4.0"),sQuery(id+"F1.wireOp",EDGE,"E21.3.5.0"),sQuery(id+"F1.wireOp",EDGE,"E21.7.5.0"),sQuery(id+"F1.wireOp",EDGE,"E21.10.5.0"),sQuery(id+"F1.wireOp",EDGE,"E21.14.5.0"),sQuery(id+"F1.wireOp",EDGE,"E21.18.5.0"),sQuery(id+"F1.wireOp",EDGE,"E21.22.5.0"),sQuery(id+"F1.wireOp",EDGE,"E21.26.5.0"),sQuery(id+"F1.wireOp",EDGE,"E21.29.5.0"),sQuery(id+"F1.wireOp",EDGE,"E22.3.6.0"),sQuery(id+"F1.wireOp",EDGE,"E22.7.6.0"),sQuery(id+"F1.wireOp",EDGE,"E22.10.6.0"),sQuery(id+"F1.wireOp",EDGE,"E22.14.6.0"),sQuery(id+"F1.wireOp",EDGE,"E22.18.6.0"),sQuery(id+"F1.wireOp",EDGE,"E22.22.6.0"),sQuery(id+"F1.wireOp",EDGE,"E22.26.6.0"),sQuery(id+"F1.wireOp",EDGE,"E22.29.6.0"),sQuery(id+"F1.wireOp",EDGE,"E22.3.7.0"),sQuery(id+"F1.wireOp",EDGE,"E22.7.7.0"),sQuery(id+"F1.wireOp",EDGE,"E22.10.7.0"),sQuery(id+"F1.wireOp",EDGE,"E22.14.7.0"),sQuery(id+"F1.wireOp",EDGE,"E22.18.7.0"),sQuery(id+"F1.wireOp",EDGE,"E22.22.7.0"),sQuery(id+"F1.wireOp",EDGE,"E22.26.7.0"),sQuery(id+"F1.wireOp",EDGE,"E22.29.7.0"),sQuery(id+"F1.wireOp",EDGE,"E22.3.8.0"),sQuery(id+"F1.wireOp",EDGE,"E22.7.8.0"),sQuery(id+"F1.wireOp",EDGE,"E22.10.8.0"),sQuery(id+"F1.wireOp",EDGE,"E22.14.8.0"),sQuery(id+"F1.wireOp",EDGE,"E22.18.8.0"),sQuery(id+"F1.wireOp",EDGE,"E22.22.8.0"),sQuery(id+"F1.wireOp",EDGE,"E22.26.8.0"),sQuery(id+"F1.wireOp",EDGE,"E22.29.8.0"),sQuery(id+"F1.wireOp",EDGE,"E22.3.9.0"),sQuery(id+"F1.wireOp",EDGE,"E22.7.9.0"),sQuery(id+"F1.wireOp",EDGE,"E22.10.9.0"),sQuery(id+"F1.wireOp",EDGE,"E22.14.9.0"),sQuery(id+"F1.wireOp",EDGE,"E22.18.9.0"),sQuery(id+"F1.wireOp",EDGE,"E22.22.9.0"),sQuery(id+"F1.wireOp",EDGE,"E22.26.9.0"),sQuery(id+"F1.wireOp",EDGE,"E22.29.9.0"),sQuery(id+"F1.wireOp",EDGE,"E22.3.10.0"),sQuery(id+"F1.wireOp",EDGE,"E22.7.10.0"),sQuery(id+"F1.wireOp",EDGE,"E22.10.10.0"),sQuery(id+"F1.wireOp",EDGE,"E22.14.10.0"),sQuery(id+"F1.wireOp",EDGE,"E22.18.10.0"),sQuery(id+"F1.wireOp",EDGE,"E22.22.10.0"),sQuery(id+"F1.wireOp",EDGE,"E22.26.10.0"),sQuery(id+"F1.wireOp",EDGE,"E22.29.10.0"),sQuery(id+"F1.wireOp",EDGE,"E22.3.11.0"),sQuery(id+"F1.wireOp",EDGE,"E22.7.11.0"),sQuery(id+"F1.wireOp",EDGE,"E22.10.11.0"),sQuery(id+"F1.wireOp",EDGE,"E22.14.11.0"),sQuery(id+"F1.wireOp",EDGE,"E22.18.11.0"),sQuery(id+"F1.wireOp",EDGE,"E22.22.11.0"),sQuery(id+"F1.wireOp",EDGE,"E22.26.11.0"),sQuery(id+"F1.wireOp",EDGE,"E22.29.11.0"),sQuery(id+"F1.wireOp",EDGE,"E22.3.12.0"),sQuery(id+"F1.wireOp",EDGE,"E22.7.12.0"),sQuery(id+"F1.wireOp",EDGE,"E22.10.12.0"),sQuery(id+"F1.wireOp",EDGE,"E22.14.12.0"),sQuery(id+"F1.wireOp",EDGE,"E22.18.12.0"),sQuery(id+"F1.wireOp",EDGE,"E22.22.12.0"),sQuery(id+"F1.wireOp",EDGE,"E22.26.12.0"),sQuery(id+"F1.wireOp",EDGE,"E22.29.12.0"),sQuery(id+"F1.wireOp",EDGE,"E22.3.13.0"),sQuery(id+"F1.wireOp",EDGE,"E22.7.13.0"),sQuery(id+"F1.wireOp",EDGE,"E22.10.13.0"),sQuery(id+"F1.wireOp",EDGE,"E22.14.13.0"),sQuery(id+"F1.wireOp",EDGE,"E22.18.13.0"),sQuery(id+"F1.wireOp",EDGE,"E22.22.13.0"),sQuery(id+"F1.wireOp",EDGE,"E22.26.13.0"),sQuery(id+"F1.wireOp",EDGE,"E22.29.13.0"),sQuery(id+"F1.wireOp",EDGE,"E22.3.14.0"),sQuery(id+"F1.wireOp",EDGE,"E22.7.14.0"),sQuery(id+"F1.wireOp",EDGE,"E22.10.14.0"),sQuery(id+"F1.wireOp",EDGE,"E22.14.14.0"),sQuery(id+"F1.wireOp",EDGE,"E22.18.14.0"),sQuery(id+"F1.wireOp",EDGE,"E22.22.14.0"),sQuery(id+"F1.wireOp",EDGE,"E22.26.14.0"),sQuery(id+"F1.wireOp",EDGE,"E22.29.14.0"),sQuery(id+"F1.wireOp",EDGE,"E22.3.15.0"),sQuery(id+"F1.wireOp",EDGE,"E22.7.15.0"),sQuery(id+"F1.wireOp",EDGE,"E22.10.15.0"),sQuery(id+"F1.wireOp",EDGE,"E22.14.15.0"),sQuery(id+"F1.wireOp",EDGE,"E22.18.15.0"),sQuery(id+"F1.wireOp",EDGE,"E22.22.15.0"),sQuery(id+"F1.wireOp",EDGE,"E22.26.15.0"),sQuery(id+"F1.wireOp",EDGE,"E22.29.15.0"),sQuery(id+"F1.wireOp",EDGE,"E22.3.16.0"),sQuery(id+"F1.wireOp",EDGE,"E22.7.16.0"),sQuery(id+"F1.wireOp",EDGE,"E22.10.16.0"),sQuery(id+"F1.wireOp",EDGE,"E22.14.16.0"),sQuery(id+"F1.wireOp",EDGE,"E22.18.16.0"),sQuery(id+"F1.wireOp",EDGE,"E22.22.16.0"),sQuery(id+"F1.wireOp",EDGE,"E22.26.16.0"),sQuery(id+"F1.wireOp",EDGE,"E22.29.16.0"),sQuery(id+"F1.wireOp",EDGE,"E22.3.17.0"),sQuery(id+"F1.wireOp",EDGE,"E22.7.17.0"),sQuery(id+"F1.wireOp",EDGE,"E22.10.17.0"),sQuery(id+"F1.wireOp",EDGE,"E22.14.17.0"),sQuery(id+"F1.wireOp",EDGE,"E22.18.17.0"),sQuery(id+"F1.wireOp",EDGE,"E22.22.17.0"),sQuery(id+"F1.wireOp",EDGE,"E22.26.17.0"),sQuery(id+"F1.wireOp",EDGE,"E22.29.17.0"),sQuery(id+"F1.wireOp",EDGE,"E22.3.18.0"),sQuery(id+"F1.wireOp",EDGE,"E22.7.18.0"),sQuery(id+"F1.wireOp",EDGE,"E22.10.18.0"),sQuery(id+"F1.wireOp",EDGE,"E22.14.18.0"),sQuery(id+"F1.wireOp",EDGE,"E22.18.18.0"),sQuery(id+"F1.wireOp",EDGE,"E22.22.18.0"),sQuery(id+"F1.wireOp",EDGE,"E22.26.18.0"),sQuery(id+"F1.wireOp",EDGE,"E22.29.18.0"),sQuery(id+"F1.wireOp",EDGE,"E22.3.19.0"),sQuery(id+"F1.wireOp",EDGE,"E22.7.19.0"),sQuery(id+"F1.wireOp",EDGE,"E22.10.19.0"),sQuery(id+"F1.wireOp",EDGE,"E22.14.19.0"),sQuery(id+"F1.wireOp",EDGE,"E22.18.19.0"),sQuery(id+"F1.wireOp",EDGE,"E22.22.19.0"),sQuery(id+"F1.wireOp",EDGE,"E22.26.19.0"),sQuery(id+"F1.wireOp",EDGE,"E22.29.19.0"),sQuery(id+"F1.wireOp",EDGE,"E22.3.20.0"),sQuery(id+"F1.wireOp",EDGE,"E22.7.20.0"),sQuery(id+"F1.wireOp",EDGE,"E22.10.20.0"),sQuery(id+"F1.wireOp",EDGE,"E22.14.20.0"),sQuery(id+"F1.wireOp",EDGE,"E22.18.20.0"),sQuery(id+"F1.wireOp",EDGE,"E22.22.20.0"),sQuery(id+"F1.wireOp",EDGE,"E22.26.20.0"),sQuery(id+"F1.wireOp",EDGE,"E22.29.20.0"),sQuery(id+"F1.wireOp",EDGE,"E22.3.21.0"),sQuery(id+"F1.wireOp",EDGE,"E22.7.21.0"),sQuery(id+"F1.wireOp",EDGE,"E22.10.21.0"),sQuery(id+"F1.wireOp",EDGE,"E22.14.21.0"),sQuery(id+"F1.wireOp",EDGE,"E22.18.21.0"),sQuery(id+"F1.wireOp",EDGE,"E22.22.21.0"),sQuery(id+"F1.wireOp",EDGE,"E22.26.21.0"),sQuery(id+"F1.wireOp",EDGE,"E22.29.21.0"),sQuery(id+"F1.wireOp",EDGE,"E22.3.22.0"),sQuery(id+"F1.wireOp",EDGE,"E22.7.22.0"),sQuery(id+"F1.wireOp",EDGE,"E22.10.22.0"),sQuery(id+"F1.wireOp",EDGE,"E22.14.22.0"),sQuery(id+"F1.wireOp",EDGE,"E22.18.22.0"),sQuery(id+"F1.wireOp",EDGE,"E22.22.22.0"),sQuery(id+"F1.wireOp",EDGE,"E22.26.22.0"),sQuery(id+"F1.wireOp",EDGE,"E22.29.22.0"),sQuery(id+"F1.wireOp",EDGE,"E22.3.23.0"),sQuery(id+"F1.wireOp",EDGE,"E22.7.23.0"),sQuery(id+"F1.wireOp",EDGE,"E22.10.23.0"),sQuery(id+"F1.wireOp",EDGE,"E22.14.23.0"),sQuery(id+"F1.wireOp",EDGE,"E22.18.23.0"),sQuery(id+"F1.wireOp",EDGE,"E22.22.23.0"),sQuery(id+"F1.wireOp",EDGE,"E22.26.23.0"),sQuery(id+"F1.wireOp",EDGE,"E22.29.23.0"),sQuery(id+"F1.wireOp",EDGE,"E22.3.24.0"),sQuery(id+"F1.wireOp",EDGE,"E22.7.24.0"),sQuery(id+"F1.wireOp",EDGE,"E22.10.24.0"),sQuery(id+"F1.wireOp",EDGE,"E22.14.24.0"),sQuery(id+"F1.wireOp",EDGE,"E22.18.24.0"),sQuery(id+"F1.wireOp",EDGE,"E22.22.24.0"),sQuery(id+"F1.wireOp",EDGE,"E22.26.24.0"),sQuery(id+"F1.wireOp",EDGE,"E22.29.24.0"),sQuery(id+"F1.wireOp",EDGE,"E22.3.25.0"),sQuery(id+"F1.wireOp",EDGE,"E22.7.25.0"),sQuery(id+"F1.wireOp",EDGE,"E22.10.25.0"),sQuery(id+"F1.wireOp",EDGE,"E22.14.25.0"),sQuery(id+"F1.wireOp",EDGE,"E22.18.25.0"),sQuery(id+"F1.wireOp",EDGE,"E22.22.25.0"),sQuery(id+"F1.wireOp",EDGE,"E22.26.25.0"),sQuery(id+"F1.wireOp",EDGE,"E22.29.25.0"),sQuery(id+"F1.wireOp",EDGE,"E22.3.26.0"),sQuery(id+"F1.wireOp",EDGE,"E22.7.26.0"),sQuery(id+"F1.wireOp",EDGE,"E22.10.26.0"),sQuery(id+"F1.wireOp",EDGE,"E22.14.26.0"),sQuery(id+"F1.wireOp",EDGE,"E22.18.26.0"),sQuery(id+"F1.wireOp",EDGE,"E22.22.26.0"),sQuery(id+"F1.wireOp",EDGE,"E22.26.26.0"),sQuery(id+"F1.wireOp",EDGE,"E22.29.26.0"),sQuery(id+"F1.wireOp",EDGE,"E22.3.27.0"),sQuery(id+"F1.wireOp",EDGE,"E22.7.27.0"),sQuery(id+"F1.wireOp",EDGE,"E22.10.27.0"),sQuery(id+"F1.wireOp",EDGE,"E22.14.27.0"),sQuery(id+"F1.wireOp",EDGE,"E22.18.27.0"),sQuery(id+"F1.wireOp",EDGE,"E22.22.27.0"),sQuery(id+"F1.wireOp",EDGE,"E22.26.27.0"),sQuery(id+"F1.wireOp",EDGE,"E22.29.27.0"),sQuery(id+"F1.wireOp",EDGE,"E22.3.28.0"),sQuery(id+"F1.wireOp",EDGE,"E22.7.28.0"),sQuery(id+"F1.wireOp",EDGE,"E22.10.28.0"),sQuery(id+"F1.wireOp",EDGE,"E22.14.28.0"),sQuery(id+"F1.wireOp",EDGE,"E22.18.28.0"),sQuery(id+"F1.wireOp",EDGE,"E22.22.28.0"),sQuery(id+"F1.wireOp",EDGE,"E22.26.28.0"),sQuery(id+"F1.wireOp",EDGE,"E22.29.28.0"),sQuery(id+"F1.wireOp",EDGE,"E22.3.29.0"),sQuery(id+"F1.wireOp",EDGE,"E22.7.29.0"),sQuery(id+"F1.wireOp",EDGE,"E22.10.29.0"),sQuery(id+"F1.wireOp",EDGE,"E22.14.29.0"),sQuery(id+"F1.wireOp",EDGE,"E22.18.29.0"),sQuery(id+"F1.wireOp",EDGE,"E22.22.29.0"),sQuery(id+"F1.wireOp",EDGE,"E22.26.29.0"),sQuery(id+"F1.wireOp",EDGE,"E22.29.29.0"),sQuery(id+"F1.wireOp",EDGE,"E23"),sQuery(id+"F1.wireOp",EDGE,"E24.trimOffspring"),sQuery(id+"F1.wireOp",EDGE,"E25.trimOffspring"),sQuery(id+"F1.wireOp",EDGE,"E26.trimOffspring"),sQuery(id+"F1.wireOp",EDGE,"E27.trimOffspring"),sQuery(id+"F1.wireOp",EDGE,"E28.trimOffspring"),sQuery(id+"F1.wireOp",EDGE,"E29.trimOffspring"),sQuery(id+"F1.wireOp",EDGE,"E30.trimOffspring"),sQuery(id+"F1.wireOp",EDGE,"E31.trimOffspring"),sQuery(id+"F1.wireOp",EDGE,"E32.trimOffspring"),sQuery(id+"F1.wireOp",EDGE,"E33.trimOffspring"),sQuery(id+"F1.wireOp",EDGE,"E34.trimOffspring"),sQuery(id+"F1.wireOp",EDGE,"E35.trimOffspring"),sQuery(id+"F1.wireOp",EDGE,"E36.trimOffspring"),sQuery(id+"F1.wireOp",EDGE,"E37.trimOffspring"),sQuery(id+"F1.wireOp",EDGE,"E38.trimOffspring"),sQuery(id+"F1.wireOp",EDGE,"E39.trimOffspring"),sQuery(id+"F1.wireOp",EDGE,"E40.trimOffspring"),sQuery(id+"F1.wireOp",EDGE,"E41.trimOffspring"),sQuery(id+"F1.wireOp",EDGE,"E42.trimOffspring"),sQuery(id+"F1.wireOp",EDGE,"E43.trimOffspring"),sQuery(id+"F1.wireOp",EDGE,"E44.trimOffspring"),sQuery(id+"F1.wireOp",EDGE,"E45.trimOffspring"),sQuery(id+"F1.wireOp",EDGE,"E46.trimOffspring"),sQuery(id+"F1.wireOp",EDGE,"E47.trimOffspring"),sQuery(id+"F1.wireOp",EDGE,"E48.trimOffspring"),sQuery(id+"F1.wireOp",EDGE,"E49.trimOffspring"),sQuery(id+"F1.wireOp",EDGE,"E50.trimOffspring"),sQuery(id+"F1.wireOp",EDGE,"E51.trimOffspring"),sQuery(id+"F1.wireOp",EDGE,"E52.trimOffspring")])],"isStart":true}),makeQuery(id+"F7.opExtrude","SWEPT_FACE",FACE,{"disambiguationData":[OSD([sQuery(id+"F6.wireOp",EDGE,"E58")])]})]});
            chamfer(context, id + "F8", {"entities" : qUnion([Q0]), "width" : 5 * mm, "tangentPropagation" : true});
        }
        {
            var Q0;
            Q0=makeQuery(id+"F4.boolean.opBoolean","INTERSECT",EDGE,{"derivedFrom":[makeQuery(id+"F2.opExtrude","SWEPT_FACE",FACE,{"disambiguationData":[OSD([sQuery(id+"F1.wireOp",EDGE,"E22.14.20.0"),sQuery(id+"F1.wireOp",EDGE,"E22.18.20.0")])]}),makeQuery(id+"F4.opRevolve","SWEPT_FACE",FACE,{"disambiguationData":[OSD([sQuery(id+"F3.wireOp",EDGE,"E53.top")])]})]});
            var Q1;
            Q1=makeQuery(id+"F4.boolean.opBoolean","INTERSECT",EDGE,{"derivedFrom":[makeQuery(id+"F2.opExtrude","SWEPT_FACE",FACE,{"disambiguationData":[OSD([sQuery(id+"F1.wireOp",EDGE,"E22.14.20.0"),sQuery(id+"F1.wireOp",EDGE,"E22.18.20.0")])]}),makeQuery(id+"F4.opRevolve","SWEPT_FACE",FACE,{"disambiguationData":[OSD([sQuery(id+"F3.wireOp",EDGE,"E53.bottom")])]})]});
            var Q2;
            Q2=makeQuery(id+"F4.boolean.opBoolean","INTERSECT",EDGE,{"derivedFrom":[makeQuery(id+"F2.opExtrude","SWEPT_FACE",FACE,{"disambiguationData":[OSD([sQuery(id+"F1.wireOp",EDGE,"E22.26.20.0")])]}),makeQuery(id+"F4.opRevolve","SWEPT_FACE",FACE,{"disambiguationData":[OSD([sQuery(id+"F3.wireOp",EDGE,"E53.top")])]})]});
            var Q3;
            Q3=makeQuery(id+"F4.boolean.opBoolean","INTERSECT",EDGE,{"derivedFrom":[makeQuery(id+"F2.opExtrude","SWEPT_FACE",FACE,{"disambiguationData":[OSD([sQuery(id+"F1.wireOp",EDGE,"E22.7.20.0")])]}),makeQuery(id+"F4.opRevolve","SWEPT_FACE",FACE,{"disambiguationData":[OSD([sQuery(id+"F3.wireOp",EDGE,"E53.top")])]})]});
            var Q4;
            Q4=makeQuery(id+"F4.boolean.opBoolean","INTERSECT",EDGE,{"derivedFrom":[makeQuery(id+"F2.opExtrude","SWEPT_FACE",FACE,{"disambiguationData":[OSD([sQuery(id+"F1.wireOp",EDGE,"E22.7.21.0")])]}),makeQuery(id+"F4.opRevolve","SWEPT_FACE",FACE,{"disambiguationData":[OSD([sQuery(id+"F3.wireOp",EDGE,"E53.top")])]})]});
            var Q5;
            Q5=makeQuery(id+"F4.boolean.opBoolean","INTERSECT",EDGE,{"derivedFrom":[makeQuery(id+"F2.opExtrude","SWEPT_FACE",FACE,{"disambiguationData":[OSD([sQuery(id+"F1.wireOp",EDGE,"E22.7.22.0")])]}),makeQuery(id+"F4.opRevolve","SWEPT_FACE",FACE,{"disambiguationData":[OSD([sQuery(id+"F3.wireOp",EDGE,"E53.top")])]})]});
            var Q6;
            Q6=makeQuery(id+"F4.boolean.opBoolean","INTERSECT",EDGE,{"derivedFrom":[makeQuery(id+"F2.opExtrude","SWEPT_FACE",FACE,{"disambiguationData":[OSD([sQuery(id+"F1.wireOp",EDGE,"E22.7.23.0")])]}),makeQuery(id+"F4.opRevolve","SWEPT_FACE",FACE,{"disambiguationData":[OSD([sQuery(id+"F3.wireOp",EDGE,"E53.top")])]})]});
            var Q7;
            Q7=makeQuery(id+"F4.boolean.opBoolean","INTERSECT",EDGE,{"derivedFrom":[makeQuery(id+"F2.opExtrude","SWEPT_FACE",FACE,{"disambiguationData":[OSD([sQuery(id+"F1.wireOp",EDGE,"E22.7.24.0")])]}),makeQuery(id+"F4.opRevolve","SWEPT_FACE",FACE,{"disambiguationData":[OSD([sQuery(id+"F3.wireOp",EDGE,"E53.top")])]})]});
            var Q8;
            Q8=makeQuery(id+"F4.boolean.opBoolean","INTERSECT",EDGE,{"derivedFrom":[makeQuery(id+"F2.opExtrude","SWEPT_FACE",FACE,{"disambiguationData":[OSD([sQuery(id+"F1.wireOp",EDGE,"E22.7.25.0")])]}),makeQuery(id+"F4.opRevolve","SWEPT_FACE",FACE,{"disambiguationData":[OSD([sQuery(id+"F3.wireOp",EDGE,"E53.top")])]})]});
            var Q9;
            Q9=makeQuery(id+"F4.boolean.opBoolean","INTERSECT",EDGE,{"derivedFrom":[makeQuery(id+"F2.opExtrude","SWEPT_FACE",FACE,{"disambiguationData":[OSD([sQuery(id+"F1.wireOp",EDGE,"E22.7.26.0")])]}),makeQuery(id+"F4.opRevolve","SWEPT_FACE",FACE,{"disambiguationData":[OSD([sQuery(id+"F3.wireOp",EDGE,"E53.top")])]})]});
            var Q10;
            Q10=makeQuery(id+"F4.boolean.opBoolean","INTERSECT",EDGE,{"derivedFrom":[makeQuery(id+"F2.opExtrude","SWEPT_FACE",FACE,{"disambiguationData":[OSD([sQuery(id+"F1.wireOp",EDGE,"E22.7.27.0")])]}),makeQuery(id+"F4.opRevolve","SWEPT_FACE",FACE,{"disambiguationData":[OSD([sQuery(id+"F3.wireOp",EDGE,"E53.top")])]})]});
            var Q11;
            Q11=makeQuery(id+"F4.boolean.opBoolean","INTERSECT",EDGE,{"derivedFrom":[makeQuery(id+"F2.opExtrude","SWEPT_FACE",FACE,{"disambiguationData":[OSD([sQuery(id+"F1.wireOp",EDGE,"E22.7.28.0")])]}),makeQuery(id+"F4.opRevolve","SWEPT_FACE",FACE,{"disambiguationData":[OSD([sQuery(id+"F3.wireOp",EDGE,"E53.top")])]})]});
            var Q12;
            Q12=makeQuery(id+"F4.boolean.opBoolean","INTERSECT",EDGE,{"derivedFrom":[makeQuery(id+"F2.opExtrude","SWEPT_FACE",FACE,{"disambiguationData":[OSD([sQuery(id+"F1.wireOp",EDGE,"E22.7.29.0")])]}),makeQuery(id+"F4.opRevolve","SWEPT_FACE",FACE,{"disambiguationData":[OSD([sQuery(id+"F3.wireOp",EDGE,"E53.top")])]})]});
            var Q13;
            Q13=makeQuery(id+"F4.boolean.opBoolean","INTERSECT",EDGE,{"derivedFrom":[makeQuery(id+"F2.opExtrude","SWEPT_FACE",FACE,{"disambiguationData":[OSD([sQuery(id+"F1.wireOp",EDGE,"E15.0")])]}),makeQuery(id+"F4.opRevolve","SWEPT_FACE",FACE,{"disambiguationData":[OSD([sQuery(id+"F3.wireOp",EDGE,"E53.top")])]})]});
            var Q14;
            Q14=makeQuery(id+"F4.boolean.opBoolean","INTERSECT",EDGE,{"derivedFrom":[makeQuery(id+"F2.opExtrude","SWEPT_FACE",FACE,{"disambiguationData":[OSD([sQuery(id+"F1.wireOp",EDGE,"E20.1.2")])]}),makeQuery(id+"F4.opRevolve","SWEPT_FACE",FACE,{"disambiguationData":[OSD([sQuery(id+"F3.wireOp",EDGE,"E53.top")])]})]});
            var Q15;
            Q15=makeQuery(id+"F4.boolean.opBoolean","INTERSECT",EDGE,{"derivedFrom":[makeQuery(id+"F2.opExtrude","SWEPT_FACE",FACE,{"disambiguationData":[OSD([sQuery(id+"F1.wireOp",EDGE,"E20.2.2")])]}),makeQuery(id+"F4.opRevolve","SWEPT_FACE",FACE,{"disambiguationData":[OSD([sQuery(id+"F3.wireOp",EDGE,"E53.top")])]})]});
            var Q16;
            Q16=makeQuery(id+"F4.boolean.opBoolean","INTERSECT",EDGE,{"derivedFrom":[makeQuery(id+"F2.opExtrude","SWEPT_FACE",FACE,{"disambiguationData":[OSD([sQuery(id+"F1.wireOp",EDGE,"E21.7.3.0")])]}),makeQuery(id+"F4.opRevolve","SWEPT_FACE",FACE,{"disambiguationData":[OSD([sQuery(id+"F3.wireOp",EDGE,"E53.top")])]})]});
            var Q17;
            Q17=makeQuery(id+"F4.boolean.opBoolean","INTERSECT",EDGE,{"derivedFrom":[makeQuery(id+"F2.opExtrude","SWEPT_FACE",FACE,{"disambiguationData":[OSD([sQuery(id+"F1.wireOp",EDGE,"E21.7.4.0")])]}),makeQuery(id+"F4.opRevolve","SWEPT_FACE",FACE,{"disambiguationData":[OSD([sQuery(id+"F3.wireOp",EDGE,"E53.top")])]})]});
            var Q18;
            Q18=makeQuery(id+"F4.boolean.opBoolean","INTERSECT",EDGE,{"derivedFrom":[makeQuery(id+"F2.opExtrude","SWEPT_FACE",FACE,{"disambiguationData":[OSD([sQuery(id+"F1.wireOp",EDGE,"E21.7.5.0")])]}),makeQuery(id+"F4.opRevolve","SWEPT_FACE",FACE,{"disambiguationData":[OSD([sQuery(id+"F3.wireOp",EDGE,"E53.top")])]})]});
            var Q19;
            Q19=makeQuery(id+"F4.boolean.opBoolean","INTERSECT",EDGE,{"derivedFrom":[makeQuery(id+"F2.opExtrude","SWEPT_FACE",FACE,{"disambiguationData":[OSD([sQuery(id+"F1.wireOp",EDGE,"E22.7.6.0")])]}),makeQuery(id+"F4.opRevolve","SWEPT_FACE",FACE,{"disambiguationData":[OSD([sQuery(id+"F3.wireOp",EDGE,"E53.top")])]})]});
            var Q20;
            Q20=makeQuery(id+"F4.boolean.opBoolean","INTERSECT",EDGE,{"derivedFrom":[makeQuery(id+"F2.opExtrude","SWEPT_FACE",FACE,{"disambiguationData":[OSD([sQuery(id+"F1.wireOp",EDGE,"E22.7.7.0")])]}),makeQuery(id+"F4.opRevolve","SWEPT_FACE",FACE,{"disambiguationData":[OSD([sQuery(id+"F3.wireOp",EDGE,"E53.top")])]})]});
            var Q21;
            Q21=makeQuery(id+"F4.boolean.opBoolean","INTERSECT",EDGE,{"derivedFrom":[makeQuery(id+"F2.opExtrude","SWEPT_FACE",FACE,{"disambiguationData":[OSD([sQuery(id+"F1.wireOp",EDGE,"E22.7.8.0")])]}),makeQuery(id+"F4.opRevolve","SWEPT_FACE",FACE,{"disambiguationData":[OSD([sQuery(id+"F3.wireOp",EDGE,"E53.top")])]})]});
            var Q22;
            Q22=makeQuery(id+"F4.boolean.opBoolean","INTERSECT",EDGE,{"derivedFrom":[makeQuery(id+"F2.opExtrude","SWEPT_FACE",FACE,{"disambiguationData":[OSD([sQuery(id+"F1.wireOp",EDGE,"E22.7.9.0")])]}),makeQuery(id+"F4.opRevolve","SWEPT_FACE",FACE,{"disambiguationData":[OSD([sQuery(id+"F3.wireOp",EDGE,"E53.top")])]})]});
            var Q23;
            Q23=makeQuery(id+"F4.boolean.opBoolean","INTERSECT",EDGE,{"derivedFrom":[makeQuery(id+"F2.opExtrude","SWEPT_FACE",FACE,{"disambiguationData":[OSD([sQuery(id+"F1.wireOp",EDGE,"E22.7.10.0")])]}),makeQuery(id+"F4.opRevolve","SWEPT_FACE",FACE,{"disambiguationData":[OSD([sQuery(id+"F3.wireOp",EDGE,"E53.top")])]})]});
            var Q24;
            Q24=makeQuery(id+"F4.boolean.opBoolean","INTERSECT",EDGE,{"derivedFrom":[makeQuery(id+"F2.opExtrude","SWEPT_FACE",FACE,{"disambiguationData":[OSD([sQuery(id+"F1.wireOp",EDGE,"E22.7.11.0")])]}),makeQuery(id+"F4.opRevolve","SWEPT_FACE",FACE,{"disambiguationData":[OSD([sQuery(id+"F3.wireOp",EDGE,"E53.top")])]})]});
            var Q25;
            Q25=makeQuery(id+"F4.boolean.opBoolean","INTERSECT",EDGE,{"derivedFrom":[makeQuery(id+"F2.opExtrude","SWEPT_FACE",FACE,{"disambiguationData":[OSD([sQuery(id+"F1.wireOp",EDGE,"E22.7.12.0")])]}),makeQuery(id+"F4.opRevolve","SWEPT_FACE",FACE,{"disambiguationData":[OSD([sQuery(id+"F3.wireOp",EDGE,"E53.top")])]})]});
            var Q26;
            Q26=makeQuery(id+"F4.boolean.opBoolean","INTERSECT",EDGE,{"derivedFrom":[makeQuery(id+"F2.opExtrude","SWEPT_FACE",FACE,{"disambiguationData":[OSD([sQuery(id+"F1.wireOp",EDGE,"E22.7.13.0")])]}),makeQuery(id+"F4.opRevolve","SWEPT_FACE",FACE,{"disambiguationData":[OSD([sQuery(id+"F3.wireOp",EDGE,"E53.top")])]})]});
            var Q27;
            Q27=makeQuery(id+"F4.boolean.opBoolean","INTERSECT",EDGE,{"derivedFrom":[makeQuery(id+"F2.opExtrude","SWEPT_FACE",FACE,{"disambiguationData":[OSD([sQuery(id+"F1.wireOp",EDGE,"E22.7.14.0")])]}),makeQuery(id+"F4.opRevolve","SWEPT_FACE",FACE,{"disambiguationData":[OSD([sQuery(id+"F3.wireOp",EDGE,"E53.top")])]})]});
            var Q28;
            Q28=makeQuery(id+"F4.boolean.opBoolean","INTERSECT",EDGE,{"derivedFrom":[makeQuery(id+"F2.opExtrude","SWEPT_FACE",FACE,{"disambiguationData":[OSD([sQuery(id+"F1.wireOp",EDGE,"E22.7.15.0")])]}),makeQuery(id+"F4.opRevolve","SWEPT_FACE",FACE,{"disambiguationData":[OSD([sQuery(id+"F3.wireOp",EDGE,"E53.top")])]})]});
            var Q29;
            Q29=makeQuery(id+"F4.boolean.opBoolean","INTERSECT",EDGE,{"derivedFrom":[makeQuery(id+"F2.opExtrude","SWEPT_FACE",FACE,{"disambiguationData":[OSD([sQuery(id+"F1.wireOp",EDGE,"E22.7.16.0")])]}),makeQuery(id+"F4.opRevolve","SWEPT_FACE",FACE,{"disambiguationData":[OSD([sQuery(id+"F3.wireOp",EDGE,"E53.top")])]})]});
            var Q30;
            Q30=makeQuery(id+"F4.boolean.opBoolean","INTERSECT",EDGE,{"derivedFrom":[makeQuery(id+"F2.opExtrude","SWEPT_FACE",FACE,{"disambiguationData":[OSD([sQuery(id+"F1.wireOp",EDGE,"E22.7.17.0")])]}),makeQuery(id+"F4.opRevolve","SWEPT_FACE",FACE,{"disambiguationData":[OSD([sQuery(id+"F3.wireOp",EDGE,"E53.top")])]})]});
            var Q31;
            Q31=makeQuery(id+"F4.boolean.opBoolean","INTERSECT",EDGE,{"derivedFrom":[makeQuery(id+"F2.opExtrude","SWEPT_FACE",FACE,{"disambiguationData":[OSD([sQuery(id+"F1.wireOp",EDGE,"E22.7.18.0")])]}),makeQuery(id+"F4.opRevolve","SWEPT_FACE",FACE,{"disambiguationData":[OSD([sQuery(id+"F3.wireOp",EDGE,"E53.top")])]})]});
            var Q32;
            Q32=makeQuery(id+"F4.boolean.opBoolean","INTERSECT",EDGE,{"derivedFrom":[makeQuery(id+"F2.opExtrude","SWEPT_FACE",FACE,{"disambiguationData":[OSD([sQuery(id+"F1.wireOp",EDGE,"E22.7.19.0")])]}),makeQuery(id+"F4.opRevolve","SWEPT_FACE",FACE,{"disambiguationData":[OSD([sQuery(id+"F3.wireOp",EDGE,"E53.top")])]})]});
            var Q33;
            Q33=makeQuery(id+"F4.boolean.opBoolean","INTERSECT",EDGE,{"derivedFrom":[makeQuery(id+"F2.opExtrude","SWEPT_FACE",FACE,{"disambiguationData":[OSD([sQuery(id+"F1.wireOp",EDGE,"E22.26.21.0")])]}),makeQuery(id+"F4.opRevolve","SWEPT_FACE",FACE,{"disambiguationData":[OSD([sQuery(id+"F3.wireOp",EDGE,"E53.top")])]})]});
            var Q34;
            Q34=makeQuery(id+"F4.boolean.opBoolean","INTERSECT",EDGE,{"derivedFrom":[makeQuery(id+"F2.opExtrude","SWEPT_FACE",FACE,{"disambiguationData":[OSD([sQuery(id+"F1.wireOp",EDGE,"E22.14.21.0"),sQuery(id+"F1.wireOp",EDGE,"E22.18.21.0")])]}),makeQuery(id+"F4.opRevolve","SWEPT_FACE",FACE,{"disambiguationData":[OSD([sQuery(id+"F3.wireOp",EDGE,"E53.top")])]})]});
            var Q35;
            Q35=makeQuery(id+"F4.boolean.opBoolean","INTERSECT",EDGE,{"derivedFrom":[makeQuery(id+"F2.opExtrude","SWEPT_FACE",FACE,{"disambiguationData":[OSD([sQuery(id+"F1.wireOp",EDGE,"E22.14.21.0"),sQuery(id+"F1.wireOp",EDGE,"E22.18.21.0")])]}),makeQuery(id+"F4.opRevolve","SWEPT_FACE",FACE,{"disambiguationData":[OSD([sQuery(id+"F3.wireOp",EDGE,"E53.bottom")])]})]});
            var Q36;
            Q36=makeQuery(id+"F4.boolean.opBoolean","INTERSECT",EDGE,{"derivedFrom":[makeQuery(id+"F2.opExtrude","SWEPT_FACE",FACE,{"disambiguationData":[OSD([sQuery(id+"F1.wireOp",EDGE,"E22.26.22.0")])]}),makeQuery(id+"F4.opRevolve","SWEPT_FACE",FACE,{"disambiguationData":[OSD([sQuery(id+"F3.wireOp",EDGE,"E53.top")])]})]});
            var Q37;
            Q37=makeQuery(id+"F4.boolean.opBoolean","INTERSECT",EDGE,{"derivedFrom":[makeQuery(id+"F2.opExtrude","SWEPT_FACE",FACE,{"disambiguationData":[OSD([sQuery(id+"F1.wireOp",EDGE,"E22.14.22.0"),sQuery(id+"F1.wireOp",EDGE,"E22.18.22.0")])]}),makeQuery(id+"F4.opRevolve","SWEPT_FACE",FACE,{"disambiguationData":[OSD([sQuery(id+"F3.wireOp",EDGE,"E53.top")])]})]});
            var Q38;
            Q38=makeQuery(id+"F4.boolean.opBoolean","INTERSECT",EDGE,{"derivedFrom":[makeQuery(id+"F2.opExtrude","SWEPT_FACE",FACE,{"disambiguationData":[OSD([sQuery(id+"F1.wireOp",EDGE,"E22.14.22.0"),sQuery(id+"F1.wireOp",EDGE,"E22.18.22.0")])]}),makeQuery(id+"F4.opRevolve","SWEPT_FACE",FACE,{"disambiguationData":[OSD([sQuery(id+"F3.wireOp",EDGE,"E53.bottom")])]})]});
            var Q39;
            Q39=makeQuery(id+"F4.boolean.opBoolean","INTERSECT",EDGE,{"derivedFrom":[makeQuery(id+"F2.opExtrude","SWEPT_FACE",FACE,{"disambiguationData":[OSD([sQuery(id+"F1.wireOp",EDGE,"E22.26.23.0")])]}),makeQuery(id+"F4.opRevolve","SWEPT_FACE",FACE,{"disambiguationData":[OSD([sQuery(id+"F3.wireOp",EDGE,"E53.top")])]})]});
            var Q40;
            Q40=makeQuery(id+"F4.boolean.opBoolean","INTERSECT",EDGE,{"derivedFrom":[makeQuery(id+"F2.opExtrude","SWEPT_FACE",FACE,{"disambiguationData":[OSD([sQuery(id+"F1.wireOp",EDGE,"E22.14.23.0"),sQuery(id+"F1.wireOp",EDGE,"E22.18.23.0")])]}),makeQuery(id+"F4.opRevolve","SWEPT_FACE",FACE,{"disambiguationData":[OSD([sQuery(id+"F3.wireOp",EDGE,"E53.top")])]})]});
            var Q41;
            Q41=makeQuery(id+"F4.boolean.opBoolean","INTERSECT",EDGE,{"derivedFrom":[makeQuery(id+"F2.opExtrude","SWEPT_FACE",FACE,{"disambiguationData":[OSD([sQuery(id+"F1.wireOp",EDGE,"E22.26.23.0")])]}),makeQuery(id+"F4.opRevolve","SWEPT_FACE",FACE,{"disambiguationData":[OSD([sQuery(id+"F3.wireOp",EDGE,"E53.bottom")])]})]});
            var Q42;
            Q42=makeQuery(id+"F4.boolean.opBoolean","INTERSECT",EDGE,{"derivedFrom":[makeQuery(id+"F2.opExtrude","SWEPT_FACE",FACE,{"disambiguationData":[OSD([sQuery(id+"F1.wireOp",EDGE,"E22.14.23.0"),sQuery(id+"F1.wireOp",EDGE,"E22.18.23.0")])]}),makeQuery(id+"F4.opRevolve","SWEPT_FACE",FACE,{"disambiguationData":[OSD([sQuery(id+"F3.wireOp",EDGE,"E53.bottom")])]})]});
            var Q43;
            Q43=makeQuery(id+"F4.boolean.opBoolean","INTERSECT",EDGE,{"derivedFrom":[makeQuery(id+"F2.opExtrude","SWEPT_FACE",FACE,{"disambiguationData":[OSD([sQuery(id+"F1.wireOp",EDGE,"E22.26.24.0")])]}),makeQuery(id+"F4.opRevolve","SWEPT_FACE",FACE,{"disambiguationData":[OSD([sQuery(id+"F3.wireOp",EDGE,"E53.bottom")])]})]});
            var Q44;
            Q44=makeQuery(id+"F4.boolean.opBoolean","INTERSECT",EDGE,{"derivedFrom":[makeQuery(id+"F2.opExtrude","SWEPT_FACE",FACE,{"disambiguationData":[OSD([sQuery(id+"F1.wireOp",EDGE,"E22.26.24.0")])]}),makeQuery(id+"F4.opRevolve","SWEPT_FACE",FACE,{"disambiguationData":[OSD([sQuery(id+"F3.wireOp",EDGE,"E53.top")])]})]});
            var Q45;
            Q45=makeQuery(id+"F4.boolean.opBoolean","INTERSECT",EDGE,{"derivedFrom":[makeQuery(id+"F2.opExtrude","SWEPT_FACE",FACE,{"disambiguationData":[OSD([sQuery(id+"F1.wireOp",EDGE,"E22.14.24.0"),sQuery(id+"F1.wireOp",EDGE,"E22.18.24.0")])]}),makeQuery(id+"F4.opRevolve","SWEPT_FACE",FACE,{"disambiguationData":[OSD([sQuery(id+"F3.wireOp",EDGE,"E53.top")])]})]});
            var Q46;
            Q46=makeQuery(id+"F4.boolean.opBoolean","INTERSECT",EDGE,{"derivedFrom":[makeQuery(id+"F2.opExtrude","SWEPT_FACE",FACE,{"disambiguationData":[OSD([sQuery(id+"F1.wireOp",EDGE,"E22.14.24.0"),sQuery(id+"F1.wireOp",EDGE,"E22.18.24.0")])]}),makeQuery(id+"F4.opRevolve","SWEPT_FACE",FACE,{"disambiguationData":[OSD([sQuery(id+"F3.wireOp",EDGE,"E53.bottom")])]})]});
            var Q47;
            Q47=makeQuery(id+"F4.boolean.opBoolean","INTERSECT",EDGE,{"derivedFrom":[makeQuery(id+"F2.opExtrude","SWEPT_FACE",FACE,{"disambiguationData":[OSD([sQuery(id+"F1.wireOp",EDGE,"E22.26.25.0")])]}),makeQuery(id+"F4.opRevolve","SWEPT_FACE",FACE,{"disambiguationData":[OSD([sQuery(id+"F3.wireOp",EDGE,"E53.top")])]})]});
            var Q48;
            Q48=makeQuery(id+"F4.boolean.opBoolean","INTERSECT",EDGE,{"derivedFrom":[makeQuery(id+"F2.opExtrude","SWEPT_FACE",FACE,{"disambiguationData":[OSD([sQuery(id+"F1.wireOp",EDGE,"E22.26.25.0")])]}),makeQuery(id+"F4.opRevolve","SWEPT_FACE",FACE,{"disambiguationData":[OSD([sQuery(id+"F3.wireOp",EDGE,"E53.bottom")])]})]});
            var Q49;
            Q49=makeQuery(id+"F4.boolean.opBoolean","INTERSECT",EDGE,{"derivedFrom":[makeQuery(id+"F2.opExtrude","SWEPT_FACE",FACE,{"disambiguationData":[OSD([sQuery(id+"F1.wireOp",EDGE,"E22.14.25.0"),sQuery(id+"F1.wireOp",EDGE,"E22.18.25.0")])]}),makeQuery(id+"F4.opRevolve","SWEPT_FACE",FACE,{"disambiguationData":[OSD([sQuery(id+"F3.wireOp",EDGE,"E53.top")])]})]});
            var Q50;
            Q50=makeQuery(id+"F4.boolean.opBoolean","INTERSECT",EDGE,{"derivedFrom":[makeQuery(id+"F2.opExtrude","SWEPT_FACE",FACE,{"disambiguationData":[OSD([sQuery(id+"F1.wireOp",EDGE,"E22.14.25.0"),sQuery(id+"F1.wireOp",EDGE,"E22.18.25.0")])]}),makeQuery(id+"F4.opRevolve","SWEPT_FACE",FACE,{"disambiguationData":[OSD([sQuery(id+"F3.wireOp",EDGE,"E53.bottom")])]})]});
            var Q51;
            Q51=makeQuery(id+"F4.boolean.opBoolean","INTERSECT",EDGE,{"derivedFrom":[makeQuery(id+"F2.opExtrude","SWEPT_FACE",FACE,{"disambiguationData":[OSD([sQuery(id+"F1.wireOp",EDGE,"E22.26.26.0")])]}),makeQuery(id+"F4.opRevolve","SWEPT_FACE",FACE,{"disambiguationData":[OSD([sQuery(id+"F3.wireOp",EDGE,"E53.top")])]})]});
            var Q52;
            Q52=makeQuery(id+"F4.boolean.opBoolean","INTERSECT",EDGE,{"derivedFrom":[makeQuery(id+"F2.opExtrude","SWEPT_FACE",FACE,{"disambiguationData":[OSD([sQuery(id+"F1.wireOp",EDGE,"E22.26.26.0")])]}),makeQuery(id+"F4.opRevolve","SWEPT_FACE",FACE,{"disambiguationData":[OSD([sQuery(id+"F3.wireOp",EDGE,"E53.bottom")])]})]});
            var Q53;
            Q53=makeQuery(id+"F4.boolean.opBoolean","INTERSECT",EDGE,{"derivedFrom":[makeQuery(id+"F2.opExtrude","SWEPT_FACE",FACE,{"disambiguationData":[OSD([sQuery(id+"F1.wireOp",EDGE,"E22.14.26.0"),sQuery(id+"F1.wireOp",EDGE,"E22.18.26.0")])]}),makeQuery(id+"F4.opRevolve","SWEPT_FACE",FACE,{"disambiguationData":[OSD([sQuery(id+"F3.wireOp",EDGE,"E53.bottom")])]})]});
            var Q54;
            Q54=makeQuery(id+"F4.boolean.opBoolean","INTERSECT",EDGE,{"derivedFrom":[makeQuery(id+"F2.opExtrude","SWEPT_FACE",FACE,{"disambiguationData":[OSD([sQuery(id+"F1.wireOp",EDGE,"E22.14.26.0"),sQuery(id+"F1.wireOp",EDGE,"E22.18.26.0")])]}),makeQuery(id+"F4.opRevolve","SWEPT_FACE",FACE,{"disambiguationData":[OSD([sQuery(id+"F3.wireOp",EDGE,"E53.top")])]})]});
            var Q55;
            Q55=makeQuery(id+"F4.boolean.opBoolean","INTERSECT",EDGE,{"derivedFrom":[makeQuery(id+"F2.opExtrude","SWEPT_FACE",FACE,{"disambiguationData":[OSD([sQuery(id+"F1.wireOp",EDGE,"E22.26.27.0")])]}),makeQuery(id+"F4.opRevolve","SWEPT_FACE",FACE,{"disambiguationData":[OSD([sQuery(id+"F3.wireOp",EDGE,"E53.top")])]})]});
            var Q56;
            Q56=makeQuery(id+"F4.boolean.opBoolean","INTERSECT",EDGE,{"derivedFrom":[makeQuery(id+"F2.opExtrude","SWEPT_FACE",FACE,{"disambiguationData":[OSD([sQuery(id+"F1.wireOp",EDGE,"E22.26.27.0")])]}),makeQuery(id+"F4.opRevolve","SWEPT_FACE",FACE,{"disambiguationData":[OSD([sQuery(id+"F3.wireOp",EDGE,"E53.bottom")])]})]});
            var Q57;
            Q57=makeQuery(id+"F4.boolean.opBoolean","INTERSECT",EDGE,{"derivedFrom":[makeQuery(id+"F2.opExtrude","SWEPT_FACE",FACE,{"disambiguationData":[OSD([sQuery(id+"F1.wireOp",EDGE,"E22.14.27.0"),sQuery(id+"F1.wireOp",EDGE,"E22.18.27.0")])]}),makeQuery(id+"F4.opRevolve","SWEPT_FACE",FACE,{"disambiguationData":[OSD([sQuery(id+"F3.wireOp",EDGE,"E53.bottom")])]})]});
            var Q58;
            Q58=makeQuery(id+"F4.boolean.opBoolean","INTERSECT",EDGE,{"derivedFrom":[makeQuery(id+"F2.opExtrude","SWEPT_FACE",FACE,{"disambiguationData":[OSD([sQuery(id+"F1.wireOp",EDGE,"E22.14.27.0"),sQuery(id+"F1.wireOp",EDGE,"E22.18.27.0")])]}),makeQuery(id+"F4.opRevolve","SWEPT_FACE",FACE,{"disambiguationData":[OSD([sQuery(id+"F3.wireOp",EDGE,"E53.top")])]})]});
            var Q59;
            Q59=makeQuery(id+"F4.boolean.opBoolean","INTERSECT",EDGE,{"derivedFrom":[makeQuery(id+"F2.opExtrude","SWEPT_FACE",FACE,{"disambiguationData":[OSD([sQuery(id+"F1.wireOp",EDGE,"E22.26.28.0")])]}),makeQuery(id+"F4.opRevolve","SWEPT_FACE",FACE,{"disambiguationData":[OSD([sQuery(id+"F3.wireOp",EDGE,"E53.top")])]})]});
            var Q60;
            Q60=makeQuery(id+"F4.boolean.opBoolean","INTERSECT",EDGE,{"derivedFrom":[makeQuery(id+"F2.opExtrude","SWEPT_FACE",FACE,{"disambiguationData":[OSD([sQuery(id+"F1.wireOp",EDGE,"E22.14.28.0"),sQuery(id+"F1.wireOp",EDGE,"E22.18.28.0")])]}),makeQuery(id+"F4.opRevolve","SWEPT_FACE",FACE,{"disambiguationData":[OSD([sQuery(id+"F3.wireOp",EDGE,"E53.bottom")])]})]});
            var Q61;
            Q61=makeQuery(id+"F4.boolean.opBoolean","INTERSECT",EDGE,{"derivedFrom":[makeQuery(id+"F2.opExtrude","SWEPT_FACE",FACE,{"disambiguationData":[OSD([sQuery(id+"F1.wireOp",EDGE,"E22.14.28.0"),sQuery(id+"F1.wireOp",EDGE,"E22.18.28.0")])]}),makeQuery(id+"F4.opRevolve","SWEPT_FACE",FACE,{"disambiguationData":[OSD([sQuery(id+"F3.wireOp",EDGE,"E53.top")])]})]});
            var Q62;
            Q62=makeQuery(id+"F4.boolean.opBoolean","INTERSECT",EDGE,{"derivedFrom":[makeQuery(id+"F2.opExtrude","SWEPT_FACE",FACE,{"disambiguationData":[OSD([sQuery(id+"F1.wireOp",EDGE,"E22.26.29.0")])]}),makeQuery(id+"F4.opRevolve","SWEPT_FACE",FACE,{"disambiguationData":[OSD([sQuery(id+"F3.wireOp",EDGE,"E53.top")])]})]});
            var Q63;
            Q63=makeQuery(id+"F4.boolean.opBoolean","INTERSECT",EDGE,{"derivedFrom":[makeQuery(id+"F2.opExtrude","SWEPT_FACE",FACE,{"disambiguationData":[OSD([sQuery(id+"F1.wireOp",EDGE,"E22.26.29.0")])]}),makeQuery(id+"F4.opRevolve","SWEPT_FACE",FACE,{"disambiguationData":[OSD([sQuery(id+"F3.wireOp",EDGE,"E53.bottom")])]})]});
            var Q64;
            Q64=makeQuery(id+"F4.boolean.opBoolean","INTERSECT",EDGE,{"derivedFrom":[makeQuery(id+"F2.opExtrude","SWEPT_FACE",FACE,{"disambiguationData":[OSD([sQuery(id+"F1.wireOp",EDGE,"E22.14.29.0"),sQuery(id+"F1.wireOp",EDGE,"E22.18.29.0")])]}),makeQuery(id+"F4.opRevolve","SWEPT_FACE",FACE,{"disambiguationData":[OSD([sQuery(id+"F3.wireOp",EDGE,"E53.bottom")])]})]});
            var Q65;
            Q65=makeQuery(id+"F4.boolean.opBoolean","INTERSECT",EDGE,{"derivedFrom":[makeQuery(id+"F2.opExtrude","SWEPT_FACE",FACE,{"disambiguationData":[OSD([sQuery(id+"F1.wireOp",EDGE,"E22.14.29.0"),sQuery(id+"F1.wireOp",EDGE,"E22.18.29.0")])]}),makeQuery(id+"F4.opRevolve","SWEPT_FACE",FACE,{"disambiguationData":[OSD([sQuery(id+"F3.wireOp",EDGE,"E53.top")])]})]});
            var Q66;
            Q66=makeQuery(id+"F4.boolean.opBoolean","INTERSECT",EDGE,{"derivedFrom":[makeQuery(id+"F2.opExtrude","SWEPT_FACE",FACE,{"disambiguationData":[OSD([sQuery(id+"F1.wireOp",EDGE,"E18.MirrorCS")])]}),makeQuery(id+"F4.opRevolve","SWEPT_FACE",FACE,{"disambiguationData":[OSD([sQuery(id+"F3.wireOp",EDGE,"E53.top")])]})]});
            var Q67;
            Q67=makeQuery(id+"F4.boolean.opBoolean","INTERSECT",EDGE,{"derivedFrom":[makeQuery(id+"F2.opExtrude","SWEPT_FACE",FACE,{"disambiguationData":[OSD([sQuery(id+"F1.wireOp",EDGE,"E18.MirrorCS")])]}),makeQuery(id+"F4.opRevolve","SWEPT_FACE",FACE,{"disambiguationData":[OSD([sQuery(id+"F3.wireOp",EDGE,"E53.bottom")])]})]});
            var Q68;
            Q68=makeQuery(id+"F4.boolean.opBoolean","INTERSECT",EDGE,{"derivedFrom":[makeQuery(id+"F2.opExtrude","SWEPT_FACE",FACE,{"disambiguationData":[OSD([sQuery(id+"F1.wireOp",EDGE,"E13.0"),sQuery(id+"F1.wireOp",EDGE,"E16.MirrorCS")])]}),makeQuery(id+"F4.opRevolve","SWEPT_FACE",FACE,{"disambiguationData":[OSD([sQuery(id+"F3.wireOp",EDGE,"E53.bottom")])]})]});
            var Q69;
            Q69=makeQuery(id+"F4.boolean.opBoolean","INTERSECT",EDGE,{"derivedFrom":[makeQuery(id+"F2.opExtrude","SWEPT_FACE",FACE,{"disambiguationData":[OSD([sQuery(id+"F1.wireOp",EDGE,"E13.0"),sQuery(id+"F1.wireOp",EDGE,"E16.MirrorCS")])]}),makeQuery(id+"F4.opRevolve","SWEPT_FACE",FACE,{"disambiguationData":[OSD([sQuery(id+"F3.wireOp",EDGE,"E53.top")])]})]});
            var Q70;
            Q70=makeQuery(id+"F4.boolean.opBoolean","COPY",FACE,{"disambiguationData":[OD(1.0)],"derivedFrom":makeQuery(id+"F4.opRevolve","SWEPT_FACE",FACE,{"disambiguationData":[OSD([sQuery(id+"F3.wireOp",EDGE,"E53.top")])]})});
            var Q71;
            Q71=makeQuery(id+"F4.boolean.opBoolean","COPY",FACE,{"disambiguationData":[OD(2.0)],"derivedFrom":makeQuery(id+"F4.opRevolve","SWEPT_FACE",FACE,{"disambiguationData":[OSD([sQuery(id+"F3.wireOp",EDGE,"E53.top")])]})});
            var Q72;
            Q72=makeQuery(id+"F4.boolean.opBoolean","INTERSECT",EDGE,{"derivedFrom":[makeQuery(id+"F2.opExtrude","SWEPT_FACE",FACE,{"disambiguationData":[OSD([sQuery(id+"F1.wireOp",EDGE,"E20.2.4"),sQuery(id+"F1.wireOp",EDGE,"E20.2.5")])]}),makeQuery(id+"F4.opRevolve","SWEPT_FACE",FACE,{"disambiguationData":[OSD([sQuery(id+"F3.wireOp",EDGE,"E53.bottom")])]})]});
            var Q73;
            Q73=makeQuery(id+"F4.boolean.opBoolean","INTERSECT",EDGE,{"derivedFrom":[makeQuery(id+"F2.opExtrude","SWEPT_FACE",FACE,{"disambiguationData":[OSD([sQuery(id+"F1.wireOp",EDGE,"E20.1.4"),sQuery(id+"F1.wireOp",EDGE,"E20.1.5")])]}),makeQuery(id+"F4.opRevolve","SWEPT_FACE",FACE,{"disambiguationData":[OSD([sQuery(id+"F3.wireOp",EDGE,"E53.bottom")])]})]});
            var Q74;
            Q74=makeQuery(id+"F4.boolean.opBoolean","INTERSECT",EDGE,{"derivedFrom":[makeQuery(id+"F2.opExtrude","SWEPT_FACE",FACE,{"disambiguationData":[OSD([sQuery(id+"F1.wireOp",EDGE,"E21.14.3.0"),sQuery(id+"F1.wireOp",EDGE,"E21.18.3.0")])]}),makeQuery(id+"F4.opRevolve","SWEPT_FACE",FACE,{"disambiguationData":[OSD([sQuery(id+"F3.wireOp",EDGE,"E53.top")])]})]});
            var Q75;
            Q75=makeQuery(id+"F4.boolean.opBoolean","INTERSECT",EDGE,{"derivedFrom":[makeQuery(id+"F2.opExtrude","SWEPT_FACE",FACE,{"disambiguationData":[OSD([sQuery(id+"F1.wireOp",EDGE,"E21.14.3.0"),sQuery(id+"F1.wireOp",EDGE,"E21.18.3.0")])]}),makeQuery(id+"F4.opRevolve","SWEPT_FACE",FACE,{"disambiguationData":[OSD([sQuery(id+"F3.wireOp",EDGE,"E53.bottom")])]})]});
            var Q76;
            Q76=makeQuery(id+"F4.boolean.opBoolean","INTERSECT",EDGE,{"derivedFrom":[makeQuery(id+"F2.opExtrude","SWEPT_FACE",FACE,{"disambiguationData":[OSD([sQuery(id+"F1.wireOp",EDGE,"E22.26.17.0")])]}),makeQuery(id+"F4.opRevolve","SWEPT_FACE",FACE,{"disambiguationData":[OSD([sQuery(id+"F3.wireOp",EDGE,"E53.top")])]})]});
            var Q77;
            Q77=makeQuery(id+"F4.boolean.opBoolean","INTERSECT",EDGE,{"derivedFrom":[makeQuery(id+"F2.opExtrude","SWEPT_FACE",FACE,{"disambiguationData":[OSD([sQuery(id+"F1.wireOp",EDGE,"E22.26.17.0")])]}),makeQuery(id+"F4.opRevolve","SWEPT_FACE",FACE,{"disambiguationData":[OSD([sQuery(id+"F3.wireOp",EDGE,"E53.bottom")])]})]});
            var Q78;
            Q78=makeQuery(id+"F4.boolean.opBoolean","INTERSECT",EDGE,{"derivedFrom":[makeQuery(id+"F2.opExtrude","SWEPT_FACE",FACE,{"disambiguationData":[OSD([sQuery(id+"F1.wireOp",EDGE,"E22.26.18.0")])]}),makeQuery(id+"F4.opRevolve","SWEPT_FACE",FACE,{"disambiguationData":[OSD([sQuery(id+"F3.wireOp",EDGE,"E53.bottom")])]})]});
            var Q79;
            Q79=makeQuery(id+"F4.boolean.opBoolean","INTERSECT",EDGE,{"derivedFrom":[makeQuery(id+"F2.opExtrude","SWEPT_FACE",FACE,{"disambiguationData":[OSD([sQuery(id+"F1.wireOp",EDGE,"E22.26.18.0")])]}),makeQuery(id+"F4.opRevolve","SWEPT_FACE",FACE,{"disambiguationData":[OSD([sQuery(id+"F3.wireOp",EDGE,"E53.top")])]})]});
            var Q80;
            Q80=makeQuery(id+"F4.boolean.opBoolean","INTERSECT",EDGE,{"derivedFrom":[makeQuery(id+"F2.opExtrude","SWEPT_FACE",FACE,{"disambiguationData":[OSD([sQuery(id+"F1.wireOp",EDGE,"E22.14.17.0"),sQuery(id+"F1.wireOp",EDGE,"E22.18.17.0")])]}),makeQuery(id+"F4.opRevolve","SWEPT_FACE",FACE,{"disambiguationData":[OSD([sQuery(id+"F3.wireOp",EDGE,"E53.top")])]})]});
            var Q81;
            Q81=makeQuery(id+"F4.boolean.opBoolean","INTERSECT",EDGE,{"derivedFrom":[makeQuery(id+"F2.opExtrude","SWEPT_FACE",FACE,{"disambiguationData":[OSD([sQuery(id+"F1.wireOp",EDGE,"E22.14.17.0"),sQuery(id+"F1.wireOp",EDGE,"E22.18.17.0")])]}),makeQuery(id+"F4.opRevolve","SWEPT_FACE",FACE,{"disambiguationData":[OSD([sQuery(id+"F3.wireOp",EDGE,"E53.bottom")])]})]});
            var Q82;
            Q82=makeQuery(id+"F4.boolean.opBoolean","INTERSECT",EDGE,{"derivedFrom":[makeQuery(id+"F2.opExtrude","SWEPT_FACE",FACE,{"disambiguationData":[OSD([sQuery(id+"F1.wireOp",EDGE,"E22.14.18.0"),sQuery(id+"F1.wireOp",EDGE,"E22.18.18.0")])]}),makeQuery(id+"F4.opRevolve","SWEPT_FACE",FACE,{"disambiguationData":[OSD([sQuery(id+"F3.wireOp",EDGE,"E53.bottom")])]})]});
            var Q83;
            Q83=makeQuery(id+"F4.boolean.opBoolean","COPY",FACE,{"disambiguationData":[OD(18.0)],"derivedFrom":makeQuery(id+"F4.opRevolve","SWEPT_FACE",FACE,{"disambiguationData":[OSD([sQuery(id+"F3.wireOp",EDGE,"E53.top")])]})});
            var Q84;
            Q84=makeQuery(id+"F4.boolean.opBoolean","COPY",FACE,{"disambiguationData":[OD(16.0)],"derivedFrom":makeQuery(id+"F4.opRevolve","SWEPT_FACE",FACE,{"disambiguationData":[OSD([sQuery(id+"F3.wireOp",EDGE,"E53.top")])]})});
            var Q85;
            Q85=makeQuery(id+"F4.boolean.opBoolean","COPY",FACE,{"disambiguationData":[OD(15.0)],"derivedFrom":makeQuery(id+"F4.opRevolve","SWEPT_FACE",FACE,{"disambiguationData":[OSD([sQuery(id+"F3.wireOp",EDGE,"E53.top")])]})});
            var Q86;
            Q86=makeQuery(id+"F4.boolean.opBoolean","COPY",FACE,{"disambiguationData":[OD(14.0)],"derivedFrom":makeQuery(id+"F4.opRevolve","SWEPT_FACE",FACE,{"disambiguationData":[OSD([sQuery(id+"F3.wireOp",EDGE,"E53.top")])]})});
            var Q87;
            Q87=makeQuery(id+"F4.boolean.opBoolean","COPY",FACE,{"disambiguationData":[OD(19.0)],"derivedFrom":makeQuery(id+"F4.opRevolve","SWEPT_FACE",FACE,{"disambiguationData":[OSD([sQuery(id+"F3.wireOp",EDGE,"E53.top")])]})});
            var Q88;
            Q88=makeQuery(id+"F4.boolean.opBoolean","COPY",FACE,{"disambiguationData":[OD(19.0)],"derivedFrom":makeQuery(id+"F4.opRevolve","SWEPT_FACE",FACE,{"disambiguationData":[OSD([sQuery(id+"F3.wireOp",EDGE,"E53.bottom")])]})});
            var Q89;
            Q89=makeQuery(id+"F4.boolean.opBoolean","COPY",FACE,{"disambiguationData":[OD(4.0)],"derivedFrom":makeQuery(id+"F4.opRevolve","SWEPT_FACE",FACE,{"disambiguationData":[OSD([sQuery(id+"F3.wireOp",EDGE,"E53.top")])]})});
            var Q90;
            Q90=makeQuery(id+"F4.boolean.opBoolean","COPY",FACE,{"disambiguationData":[OD(5.0)],"derivedFrom":makeQuery(id+"F4.opRevolve","SWEPT_FACE",FACE,{"disambiguationData":[OSD([sQuery(id+"F3.wireOp",EDGE,"E53.top")])]})});
            var Q91;
            Q91=makeQuery(id+"F4.boolean.opBoolean","COPY",FACE,{"disambiguationData":[OD(6.0)],"derivedFrom":makeQuery(id+"F4.opRevolve","SWEPT_FACE",FACE,{"disambiguationData":[OSD([sQuery(id+"F3.wireOp",EDGE,"E53.top")])]})});
            var Q92;
            Q92=makeQuery(id+"F4.boolean.opBoolean","COPY",FACE,{"disambiguationData":[OD(7.0)],"derivedFrom":makeQuery(id+"F4.opRevolve","SWEPT_FACE",FACE,{"disambiguationData":[OSD([sQuery(id+"F3.wireOp",EDGE,"E53.top")])]})});
            var Q93;
            Q93=makeQuery(id+"F4.boolean.opBoolean","COPY",FACE,{"disambiguationData":[OD(8.0)],"derivedFrom":makeQuery(id+"F4.opRevolve","SWEPT_FACE",FACE,{"disambiguationData":[OSD([sQuery(id+"F3.wireOp",EDGE,"E53.top")])]})});
            var Q94;
            Q94=makeQuery(id+"F4.boolean.opBoolean","COPY",FACE,{"disambiguationData":[OD(9.0)],"derivedFrom":makeQuery(id+"F4.opRevolve","SWEPT_FACE",FACE,{"disambiguationData":[OSD([sQuery(id+"F3.wireOp",EDGE,"E53.top")])]})});
            var Q95;
            Q95=makeQuery(id+"F4.boolean.opBoolean","COPY",FACE,{"disambiguationData":[OD(10.0)],"derivedFrom":makeQuery(id+"F4.opRevolve","SWEPT_FACE",FACE,{"disambiguationData":[OSD([sQuery(id+"F3.wireOp",EDGE,"E53.top")])]})});
            var Q96;
            Q96=makeQuery(id+"F4.boolean.opBoolean","COPY",FACE,{"disambiguationData":[OD(11.0)],"derivedFrom":makeQuery(id+"F4.opRevolve","SWEPT_FACE",FACE,{"disambiguationData":[OSD([sQuery(id+"F3.wireOp",EDGE,"E53.top")])]})});
            var Q97;
            Q97=makeQuery(id+"F4.boolean.opBoolean","COPY",FACE,{"disambiguationData":[OD(12.0)],"derivedFrom":makeQuery(id+"F4.opRevolve","SWEPT_FACE",FACE,{"disambiguationData":[OSD([sQuery(id+"F3.wireOp",EDGE,"E53.top")])]})});
            var Q98;
            Q98=makeQuery(id+"F4.boolean.opBoolean","COPY",FACE,{"disambiguationData":[OD(13.0)],"derivedFrom":makeQuery(id+"F4.opRevolve","SWEPT_FACE",FACE,{"disambiguationData":[OSD([sQuery(id+"F3.wireOp",EDGE,"E53.top")])]})});
            var Q99;
            Q99=makeQuery(id+"F4.boolean.opBoolean","COPY",FACE,{"disambiguationData":[OD(13.0)],"derivedFrom":makeQuery(id+"F4.opRevolve","SWEPT_FACE",FACE,{"disambiguationData":[OSD([sQuery(id+"F3.wireOp",EDGE,"E53.bottom")])]})});
            var Q100;
            Q100=makeQuery(id+"F4.boolean.opBoolean","COPY",FACE,{"disambiguationData":[OD(14.0)],"derivedFrom":makeQuery(id+"F4.opRevolve","SWEPT_FACE",FACE,{"disambiguationData":[OSD([sQuery(id+"F3.wireOp",EDGE,"E53.bottom")])]})});
            var Q101;
            Q101=makeQuery(id+"F4.boolean.opBoolean","COPY",FACE,{"disambiguationData":[OD(15.0)],"derivedFrom":makeQuery(id+"F4.opRevolve","SWEPT_FACE",FACE,{"disambiguationData":[OSD([sQuery(id+"F3.wireOp",EDGE,"E53.bottom")])]})});
            var Q102;
            Q102=makeQuery(id+"F4.boolean.opBoolean","COPY",FACE,{"disambiguationData":[OD(16.0)],"derivedFrom":makeQuery(id+"F4.opRevolve","SWEPT_FACE",FACE,{"disambiguationData":[OSD([sQuery(id+"F3.wireOp",EDGE,"E53.bottom")])]})});
            var Q103;
            Q103=makeQuery(id+"F4.boolean.opBoolean","COPY",FACE,{"disambiguationData":[OD(11.0)],"derivedFrom":makeQuery(id+"F4.opRevolve","SWEPT_FACE",FACE,{"disambiguationData":[OSD([sQuery(id+"F3.wireOp",EDGE,"E53.bottom")])]})});
            var Q104;
            Q104=makeQuery(id+"F4.boolean.opBoolean","COPY",FACE,{"disambiguationData":[OD(12.0)],"derivedFrom":makeQuery(id+"F4.opRevolve","SWEPT_FACE",FACE,{"disambiguationData":[OSD([sQuery(id+"F3.wireOp",EDGE,"E53.bottom")])]})});
            var Q105;
            Q105=makeQuery(id+"F4.boolean.opBoolean","COPY",FACE,{"disambiguationData":[OD(9.0)],"derivedFrom":makeQuery(id+"F4.opRevolve","SWEPT_FACE",FACE,{"disambiguationData":[OSD([sQuery(id+"F3.wireOp",EDGE,"E53.bottom")])]})});
            var Q106;
            Q106=makeQuery(id+"F4.boolean.opBoolean","COPY",FACE,{"disambiguationData":[OD(10.0)],"derivedFrom":makeQuery(id+"F4.opRevolve","SWEPT_FACE",FACE,{"disambiguationData":[OSD([sQuery(id+"F3.wireOp",EDGE,"E53.bottom")])]})});
            var Q107;
            Q107=makeQuery(id+"F4.boolean.opBoolean","COPY",FACE,{"disambiguationData":[OD(8.0)],"derivedFrom":makeQuery(id+"F4.opRevolve","SWEPT_FACE",FACE,{"disambiguationData":[OSD([sQuery(id+"F3.wireOp",EDGE,"E53.bottom")])]})});
            var Q108;
            Q108=makeQuery(id+"F4.boolean.opBoolean","COPY",FACE,{"disambiguationData":[OD(7.0)],"derivedFrom":makeQuery(id+"F4.opRevolve","SWEPT_FACE",FACE,{"disambiguationData":[OSD([sQuery(id+"F3.wireOp",EDGE,"E53.bottom")])]})});
            var Q109;
            Q109=makeQuery(id+"F4.boolean.opBoolean","COPY",FACE,{"disambiguationData":[OD(6.0)],"derivedFrom":makeQuery(id+"F4.opRevolve","SWEPT_FACE",FACE,{"disambiguationData":[OSD([sQuery(id+"F3.wireOp",EDGE,"E53.bottom")])]})});
            var Q110;
            Q110=makeQuery(id+"F4.boolean.opBoolean","COPY",FACE,{"disambiguationData":[OD(5.0)],"derivedFrom":makeQuery(id+"F4.opRevolve","SWEPT_FACE",FACE,{"disambiguationData":[OSD([sQuery(id+"F3.wireOp",EDGE,"E53.bottom")])]})});
            var Q111;
            Q111=makeQuery(id+"F4.boolean.opBoolean","COPY",FACE,{"disambiguationData":[OD(4.0)],"derivedFrom":makeQuery(id+"F4.opRevolve","SWEPT_FACE",FACE,{"disambiguationData":[OSD([sQuery(id+"F3.wireOp",EDGE,"E53.bottom")])]})});
            var Q112;
            Q112=makeQuery(id+"F4.boolean.opBoolean","COPY",FACE,{"disambiguationData":[OD(3.0)],"derivedFrom":makeQuery(id+"F4.opRevolve","SWEPT_FACE",FACE,{"disambiguationData":[OSD([sQuery(id+"F3.wireOp",EDGE,"E53.bottom")])]})});
            chamfer(context, id + "F9", {"entities" : qUnion([Q0, Q1, Q2, Q3, Q4, Q5, Q6, Q7, Q8, Q9, Q10, Q11, Q12, Q13, Q14, Q15, Q16, Q17, Q18, Q19, Q20, Q21, Q22, Q23, Q24, Q25, Q26, Q27, Q28, Q29, Q30, Q31, Q32, Q33, Q34, Q35, Q36, Q37, Q38, Q39, Q40, Q41, Q42, Q43, Q44, Q45, Q46, Q47, Q48, Q49, Q50, Q51, Q52, Q53, Q54, Q55, Q56, Q57, Q58, Q59, Q60, Q61, Q62, Q63, Q64, Q65, Q66, Q67, Q68, Q69, Q70, Q71, Q72, Q73, Q74, Q75, Q76, Q77, Q78, Q79, Q80, Q81, Q82, Q83, Q84, Q85, Q86, Q87, Q88, Q89, Q90, Q91, Q92, Q93, Q94, Q95, Q96, Q97, Q98, Q99, Q100, Q101, Q102, Q103, Q104, Q105, Q106, Q107, Q108, Q109, Q110, Q111, Q112]), "chamferType" : ChamferType.OFFSET_ANGLE, "width" : 2.5 * mm, "oppositeDirection" : false, "angle" : 45 * degree, "tangentPropagation" : true});
        }
    });
